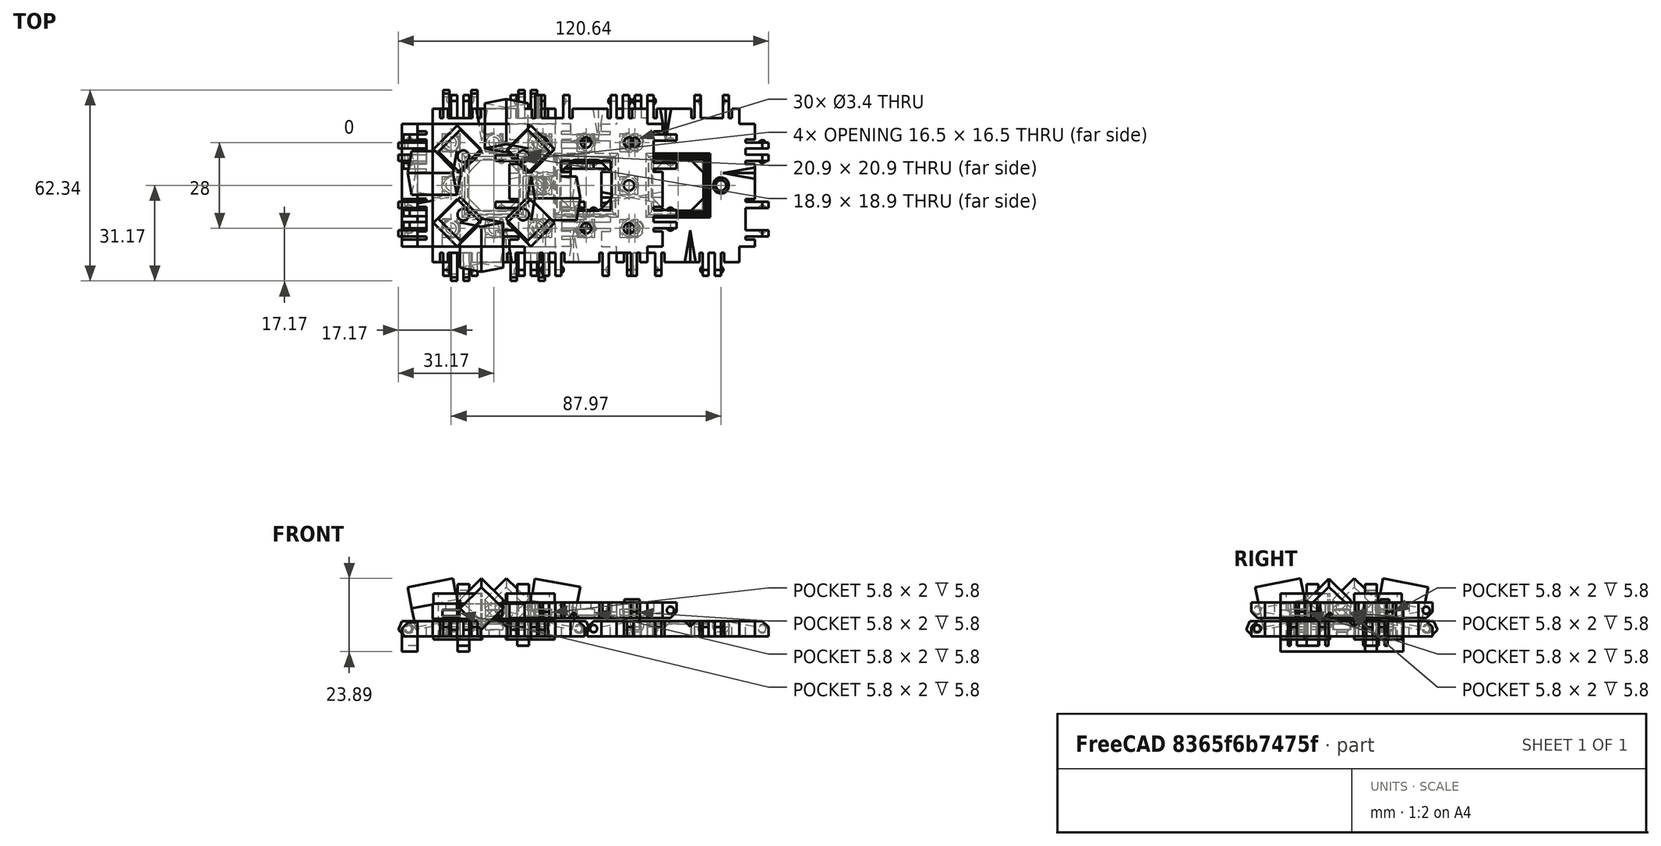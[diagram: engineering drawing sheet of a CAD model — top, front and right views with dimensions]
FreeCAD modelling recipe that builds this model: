
FCSTD DOCUMENT  (FreeCAD 0.17R13522 (Git))
Label: Robot Plates 0.6
License: All rights reserved
LicenseURL: http://en.wikipedia.org/wiki/All_rights_reserved
objects: Part::Box×402, Part::Cut×142, Part::Sphere×126, Part::MultiFuse×90, Part::Fuse×55, Part::Cylinder×40, Part::Chamfer×15, App::DocumentObjectGroup×2, Drawing::FeatureViewAnnotation×2, Drawing::FeaturePage×1
note: 870 computed .brp shape members not serialized (recipe doc carries the construction recipe); baked Part::Feature solids carry a one-line shape summary decoded from their .brp

FEATURE [Part::Box] Box  label="Cube"
  AttacherType = Attacher::AttachEngine3D
  Height = 5
  Length = 40
  Placement = pos=(0,0,-2) rot=(0,0,1;0rad)
  Width = 40
FEATURE [Part::Sphere] Sphere003  label="Mag Hole 3"
  Angle1 = -90
  Angle2 = 90
  Angle3 = 360
  AttacherType = Attacher::AttachEngine3D
  Placement = pos=(6,34,1.7) rot=(0,0,1;0rad)
  Radius = 2.85
FEATURE [Part::Sphere] Sphere005  label="Mag Hole 2"
  Angle1 = -90
  Angle2 = 90
  Angle3 = 360
  AttacherType = Attacher::AttachEngine3D
  Placement = pos=(34,20,1.7) rot=(0,0,1;0rad)
  Radius = 2.85
FEATURE [Part::Sphere] Sphere  label="Mag Hole"
  Angle1 = -90
  Angle2 = 90
  Angle3 = 360
  AttacherType = Attacher::AttachEngine3D
  Placement = pos=(6,6,1.7) rot=(0,0,1;0rad)
  Radius = 2.85
FEATURE [Part::MultiFuse] Fusion004
  Shapes = -> [Sphere,Sphere005,Sphere003]
FEATURE [Part::Cut] Cut003
  Base = -> Box
  Tool = -> Fusion004
FEATURE [Part::Box] Box001  label="Cube001"
  AttacherType = Attacher::AttachEngine3D
  Height = 7
  Length = 5
  Placement = pos=(-5,0,-2) rot=(0,0,1;0rad)
  Width = 40
FEATURE [Part::Box] Box002  label="Cube002"
  AttacherType = Attacher::AttachEngine3D
  Height = 7
  Length = 10
  Placement = pos=(-15,6,-2) rot=(0,0,1;0rad)
  Width = 2
FEATURE [Part::Box] Box003  label="Cube003"
  AttacherType = Attacher::AttachEngine3D
  Height = 7
  Length = 10
  Placement = pos=(-15,10,-2) rot=(0,0,1;0rad)
  Width = 2
FEATURE [Part::Box] Box004  label="Cube004"
  AttacherType = Attacher::AttachEngine3D
  Height = 7
  Length = 10
  Placement = pos=(-15,25.4,-2) rot=(0,0,1;0rad)
  Width = 2
FEATURE [Part::Box] Box005  label="Cube005"
  AttacherType = Attacher::AttachEngine3D
  Height = 7
  Length = 10
  Placement = pos=(-15,34.6,-2) rot=(0,0,1;0rad)
  Width = 2
FEATURE [Part::Sphere] Sphere008
  Angle1 = -90
  Angle2 = 90
  Angle3 = 360
  AttacherType = Attacher::AttachEngine3D
  Placement = pos=(-7.5,6.5,0.5) rot=(0,0,1;0rad)
  Radius = 1.25
FEATURE [Part::Box] Box006  label="Chamfer Cube"
  AttacherType = Attacher::AttachEngine3D
  Height = 10
  Length = 13
  Placement = pos=(-11.69,0,-1.19) rot=(0,-1,0;0.785398rad)
  Width = 40
FEATURE [Part::Sphere] Sphere009
  Angle1 = -90
  Angle2 = 90
  Angle3 = 360
  AttacherType = Attacher::AttachEngine3D
  Placement = pos=(-7.5,11.5,0.5) rot=(0,0,1;0rad)
  Radius = 1.25
FEATURE [Part::Sphere] Sphere010
  Angle1 = -90
  Angle2 = 90
  Angle3 = 360
  AttacherType = Attacher::AttachEngine3D
  Placement = pos=(-7.5,28,0.5) rot=(0,0,1;0rad)
  Radius = 1.5
FEATURE [Part::Sphere] Sphere011
  Angle1 = -90
  Angle2 = 90
  Angle3 = 360
  AttacherType = Attacher::AttachEngine3D
  Placement = pos=(-7.5,34,0.5) rot=(0,0,1;0rad)
  Radius = 1.5
FEATURE [Part::Box] Box007  label="Cube007"
  AttacherType = Attacher::AttachEngine3D
  Height = 7
  Length = 4
  Placement = pos=(-6,5,-2) rot=(0,0,1;0rad)
  Width = 1
FEATURE [Part::Box] Box008  label="Cube008"
  AttacherType = Attacher::AttachEngine3D
  Height = 7
  Length = 4
  Placement = pos=(-6,8,-2) rot=(0,0,1;0rad)
  Width = 2
FEATURE [Part::Box] Box009  label="Cube009"
  AttacherType = Attacher::AttachEngine3D
  Height = 7
  Length = 4
  Placement = pos=(-6,12,-2) rot=(0,0,1;0rad)
  Width = 1
FEATURE [Part::Box] Box010  label="Cube010"
  AttacherType = Attacher::AttachEngine3D
  Height = 7
  Length = 4
  Placement = pos=(-6,24.4,-2) rot=(0,0,1;0rad)
  Width = 1
FEATURE [Part::Box] Box011  label="Cube011"
  AttacherType = Attacher::AttachEngine3D
  Height = 7
  Length = 4
  Placement = pos=(-6,36.6,-2) rot=(0,0,1;0rad)
  Width = 1
FEATURE [Part::Box] Box012  label="Cube012"
  AttacherType = Attacher::AttachEngine3D
  Height = 7
  Length = 4
  Placement = pos=(-6,27.4,-2) rot=(0,0,1;0rad)
  Width = 7.2
FEATURE [Part::MultiFuse] Fusion003  label="Extra Holes for Clips"
  Shapes = -> [Box012,Box009,Box011,Box008,Box010,Box007]
FEATURE [Part::Box] Box013  label="Re-level Edge Clip Block"
  AttacherType = Attacher::AttachEngine3D
  Height = 10
  Length = 20
  Placement = pos=(-19,-2,3) rot=(0,0,1;0rad)
  Width = 44
FEATURE [Part::Box] Box014  label="Cube014"
  AttacherType = Attacher::AttachEngine3D
  Height = 7
  Length = 10
  Placement = pos=(-10,34.6,0) rot=(0,0,1;0rad)
  Width = 2
FEATURE [Part::Box] Box015  label="Cube015"
  AttacherType = Attacher::AttachEngine3D
  Height = 7
  Length = 5
  Width = 40
FEATURE [Part::Box] Box016  label="Cube016"
  AttacherType = Attacher::AttachEngine3D
  Height = 7
  Length = 10
  Placement = pos=(-10,25.4,0) rot=(0,0,1;0rad)
  Width = 2
FEATURE [Part::Box] Box017  label="Cube017"
  AttacherType = Attacher::AttachEngine3D
  Height = 7
  Length = 10
  Placement = pos=(-10,10,0) rot=(0,0,1;0rad)
  Width = 2
FEATURE [Part::Box] Box018  label="Cube018"
  AttacherType = Attacher::AttachEngine3D
  Height = 7
  Length = 10
  Placement = pos=(-10,6,0) rot=(0,0,1;0rad)
  Width = 2
FEATURE [Part::Sphere] Sphere012
  Angle1 = -90
  Angle2 = 90
  Angle3 = 360
  AttacherType = Attacher::AttachEngine3D
  Placement = pos=(-3,6.5,2.5) rot=(0,0,1;0rad)
  Radius = 1.25
FEATURE [Part::Box] Box019  label="Cube019"
  AttacherType = Attacher::AttachEngine3D
  Height = 10
  Length = 13
  Placement = pos=(-10.19,0,-1.19) rot=(0,-1,0;0.785398rad)
  Width = 40
FEATURE [Part::Sphere] Sphere013
  Angle1 = -90
  Angle2 = 90
  Angle3 = 360
  AttacherType = Attacher::AttachEngine3D
  Placement = pos=(-3,11.5,2.5) rot=(0,0,1;0rad)
  Radius = 1.25
FEATURE [Part::Sphere] Sphere014
  Angle1 = -90
  Angle2 = 90
  Angle3 = 360
  AttacherType = Attacher::AttachEngine3D
  Placement = pos=(-3,28,2.5) rot=(0,0,1;0rad)
  Radius = 1.5
FEATURE [Part::Sphere] Sphere015
  Angle1 = -90
  Angle2 = 90
  Angle3 = 360
  AttacherType = Attacher::AttachEngine3D
  Placement = pos=(-3,34,2.5) rot=(0,0,1;0rad)
  Radius = 1.5
FEATURE [Part::MultiFuse] Fusion005
  Shapes = -> [Box015,Box018,Box017,Box016,Box014]
FEATURE [Part::Cut] Cut005
  Base = -> Fusion005
  Tool = -> Box019
FEATURE [Part::MultiFuse] Fusion006
  Shapes = -> [Sphere012,Sphere013,Cut005]
FEATURE [Part::MultiFuse] Fusion007
  Shapes = -> [Sphere015,Sphere014]
FEATURE [Part::Cut] Cut006
  Base = -> Fusion006
  Tool = -> Fusion007
FEATURE [Part::Chamfer] Chamfer002
  Base = -> Cut006
  Edges = 4 edges r=4: [Edge31,Edge37,Edge43,Edge46]
FEATURE [Part::Box] Box020  label="Cube020"
  AttacherType = Attacher::AttachEngine3D
  Height = 7
  Length = 4
  Placement = pos=(-1,5,0) rot=(0,0,1;0rad)
  Width = 1
FEATURE [Part::Box] Box021  label="Cube021"
  AttacherType = Attacher::AttachEngine3D
  Height = 7
  Length = 4
  Placement = pos=(-1,8,0) rot=(0,0,1;0rad)
  Width = 2
FEATURE [Part::Box] Box022  label="Cube022"
  AttacherType = Attacher::AttachEngine3D
  Height = 7
  Length = 4
  Placement = pos=(-1,12,0) rot=(0,0,1;0rad)
  Width = 1
FEATURE [Part::Box] Box023  label="Cube023"
  AttacherType = Attacher::AttachEngine3D
  Height = 7
  Length = 4
  Placement = pos=(-1,24.4,0) rot=(0,0,1;0rad)
  Width = 1
FEATURE [Part::Box] Box024  label="Cube024"
  AttacherType = Attacher::AttachEngine3D
  Height = 7
  Length = 4
  Placement = pos=(-1,36.6,0) rot=(0,0,1;0rad)
  Width = 1
FEATURE [Part::Box] Box025  label="Cube025"
  AttacherType = Attacher::AttachEngine3D
  Height = 7
  Length = 4
  Placement = pos=(-1,27.4,0) rot=(0,0,1;0rad)
  Width = 7.2
FEATURE [Part::MultiFuse] Fusion008
  Shapes = -> [Box025,Box022,Box024,Box021,Box023,Box020]
FEATURE [Part::Cut] Cut007
  Base = -> Chamfer002
  Placement = pos=(-5,40,3) rot=(1,0,0;3.14159rad)
  Tool = -> Fusion008
FEATURE [Part::Box] Box026  label="Cube026"
  AttacherType = Attacher::AttachEngine3D
  Height = 10
  Length = 12
  Placement = pos=(-11,-2,-12) rot=(0,0,1;0rad)
  Width = 44
FEATURE [Part::Cut] Cut008
  Base = -> Cut007
  Placement = pos=(40,0,0) rot=(0,0,1;1.5708rad)
  Tool = -> Box026
FEATURE [Part::Box] Box027  label="Cube027"
  AttacherType = Attacher::AttachEngine3D
  Height = 7
  Length = 4
  Placement = pos=(-1,12,0) rot=(0,0,1;0rad)
  Width = 1
FEATURE [Part::Box] Box028  label="Cube028"
  AttacherType = Attacher::AttachEngine3D
  Height = 10
  Length = 13
  Placement = pos=(-10.19,0,-1.19) rot=(0,-1,0;0.785398rad)
  Width = 40
FEATURE [Part::Box] Box029  label="Cube029"
  AttacherType = Attacher::AttachEngine3D
  Height = 7
  Length = 4
  Placement = pos=(-1,27.4,0) rot=(0,0,1;0rad)
  Width = 7.2
FEATURE [Part::Box] Box030  label="Cube030"
  AttacherType = Attacher::AttachEngine3D
  Height = 7
  Length = 4
  Placement = pos=(-1,5,0) rot=(0,0,1;0rad)
  Width = 1
FEATURE [Part::Box] Box031  label="Cube031"
  AttacherType = Attacher::AttachEngine3D
  Height = 7
  Length = 10
  Placement = pos=(-10,6,0) rot=(0,0,1;0rad)
  Width = 2
FEATURE [Part::Box] Box032  label="Cube032"
  AttacherType = Attacher::AttachEngine3D
  Height = 10
  Length = 12
  Placement = pos=(-11,-2,-12) rot=(0,0,1;0rad)
  Width = 44
FEATURE [Part::Sphere] Sphere016
  Angle1 = -90
  Angle2 = 90
  Angle3 = 360
  AttacherType = Attacher::AttachEngine3D
  Placement = pos=(-3,6.5,2.5) rot=(0,0,1;0rad)
  Radius = 1.25
FEATURE [Part::Box] Box033  label="Cube033"
  AttacherType = Attacher::AttachEngine3D
  Height = 7
  Length = 10
  Placement = pos=(-10,25.4,0) rot=(0,0,1;0rad)
  Width = 2
FEATURE [Part::Box] Box034  label="Cube034"
  AttacherType = Attacher::AttachEngine3D
  Height = 7
  Length = 10
  Placement = pos=(-10,10,0) rot=(0,0,1;0rad)
  Width = 2
FEATURE [Part::Sphere] Sphere017
  Angle1 = -90
  Angle2 = 90
  Angle3 = 360
  AttacherType = Attacher::AttachEngine3D
  Placement = pos=(-3,28,2.5) rot=(0,0,1;0rad)
  Radius = 1.5
FEATURE [Part::Sphere] Sphere018
  Angle1 = -90
  Angle2 = 90
  Angle3 = 360
  AttacherType = Attacher::AttachEngine3D
  Placement = pos=(-3,11.5,2.5) rot=(0,0,1;0rad)
  Radius = 1.25
FEATURE [Part::Box] Box035  label="Cube035"
  AttacherType = Attacher::AttachEngine3D
  Height = 7
  Length = 4
  Placement = pos=(-1,36.6,0) rot=(0,0,1;0rad)
  Width = 1
FEATURE [Part::Sphere] Sphere019
  Angle1 = -90
  Angle2 = 90
  Angle3 = 360
  AttacherType = Attacher::AttachEngine3D
  Placement = pos=(-3,34,2.5) rot=(0,0,1;0rad)
  Radius = 1.5
FEATURE [Part::MultiFuse] Fusion011
  Shapes = -> [Sphere019,Sphere017]
FEATURE [Part::Box] Box036  label="Cube036"
  AttacherType = Attacher::AttachEngine3D
  Height = 7
  Length = 4
  Placement = pos=(-1,8,0) rot=(0,0,1;0rad)
  Width = 2
FEATURE [Part::Box] Box037  label="Cube037"
  AttacherType = Attacher::AttachEngine3D
  Height = 7
  Length = 10
  Placement = pos=(-10,34.6,0) rot=(0,0,1;0rad)
  Width = 2
FEATURE [Part::Box] Box038  label="Cube038"
  AttacherType = Attacher::AttachEngine3D
  Height = 7
  Length = 4
  Placement = pos=(-1,24.4,0) rot=(0,0,1;0rad)
  Width = 1
FEATURE [Part::MultiFuse] Fusion009
  Shapes = -> [Box029,Box027,Box035,Box036,Box038,Box030]
FEATURE [Part::Box] Box039  label="Cube039"
  AttacherType = Attacher::AttachEngine3D
  Height = 7
  Length = 5
  Width = 40
FEATURE [Part::MultiFuse] Fusion012
  Shapes = -> [Box039,Box031,Box034,Box033,Box037]
FEATURE [Part::Cut] Cut011
  Base = -> Fusion012
  Tool = -> Box028
FEATURE [Part::MultiFuse] Fusion010
  Shapes = -> [Sphere016,Sphere018,Cut011]
FEATURE [Part::Cut] Cut012
  Base = -> Fusion010
  Tool = -> Fusion011
FEATURE [Part::Chamfer] Chamfer003
  Base = -> Cut012
  Edges = 4 edges r=4: [Edge31,Edge37,Edge43,Edge46]
FEATURE [Part::Cut] Cut010
  Base = -> Chamfer003
  Placement = pos=(-5,40,3) rot=(1,0,0;3.14159rad)
  Tool = -> Fusion009
FEATURE [Part::Cut] Cut009
  Base = -> Cut010
  Placement = pos=(40,40,0) rot=(0,0,1;3.14159rad)
  Tool = -> Box032
FEATURE [Part::Sphere] Sphere020
  Angle1 = -90
  Angle2 = 90
  Angle3 = 360
  AttacherType = Attacher::AttachEngine3D
  Placement = pos=(-3,11.5,2.5) rot=(0,0,1;0rad)
  Radius = 1.25
FEATURE [Part::Box] Box040  label="Cube040"
  AttacherType = Attacher::AttachEngine3D
  Height = 7
  Length = 10
  Placement = pos=(-10,6,0) rot=(0,0,1;0rad)
  Width = 2
FEATURE [Part::Box] Box041  label="Cube041"
  AttacherType = Attacher::AttachEngine3D
  Height = 7
  Length = 4
  Placement = pos=(-1,8,0) rot=(0,0,1;0rad)
  Width = 2
FEATURE [Part::Box] Box042  label="Cube042"
  AttacherType = Attacher::AttachEngine3D
  Height = 7
  Length = 10
  Placement = pos=(-10,10,0) rot=(0,0,1;0rad)
  Width = 2
FEATURE [Part::Box] Box043  label="Cube043"
  AttacherType = Attacher::AttachEngine3D
  Height = 10
  Length = 12
  Placement = pos=(-11,-2,-12) rot=(0,0,1;0rad)
  Width = 44
FEATURE [Part::Box] Box044  label="Cube044"
  AttacherType = Attacher::AttachEngine3D
  Height = 7
  Length = 4
  Placement = pos=(-1,5,0) rot=(0,0,1;0rad)
  Width = 1
FEATURE [Part::Sphere] Sphere021
  Angle1 = -90
  Angle2 = 90
  Angle3 = 360
  AttacherType = Attacher::AttachEngine3D
  Placement = pos=(-3,28,2.5) rot=(0,0,1;0rad)
  Radius = 1.5
FEATURE [Part::Sphere] Sphere022
  Angle1 = -90
  Angle2 = 90
  Angle3 = 360
  AttacherType = Attacher::AttachEngine3D
  Placement = pos=(-3,6.5,2.5) rot=(0,0,1;0rad)
  Radius = 1.25
FEATURE [Part::Sphere] Sphere023
  Angle1 = -90
  Angle2 = 90
  Angle3 = 360
  AttacherType = Attacher::AttachEngine3D
  Placement = pos=(-3,34,2.5) rot=(0,0,1;0rad)
  Radius = 1.5
FEATURE [Part::Box] Box045  label="Cube045"
  AttacherType = Attacher::AttachEngine3D
  Height = 7
  Length = 4
  Placement = pos=(-1,12,0) rot=(0,0,1;0rad)
  Width = 1
FEATURE [Part::Box] Box046  label="Cube046"
  AttacherType = Attacher::AttachEngine3D
  Height = 7
  Length = 5
  Width = 40
FEATURE [Part::Box] Box047  label="Cube047"
  AttacherType = Attacher::AttachEngine3D
  Height = 7
  Length = 4
  Placement = pos=(-1,36.6,0) rot=(0,0,1;0rad)
  Width = 1
FEATURE [Part::Box] Box048  label="Cube048"
  AttacherType = Attacher::AttachEngine3D
  Height = 7
  Length = 4
  Placement = pos=(-1,24.4,0) rot=(0,0,1;0rad)
  Width = 1
FEATURE [Part::Box] Box049  label="Cube049"
  AttacherType = Attacher::AttachEngine3D
  Height = 7
  Length = 10
  Placement = pos=(-10,25.4,0) rot=(0,0,1;0rad)
  Width = 2
FEATURE [Part::Box] Box050  label="Cube050"
  AttacherType = Attacher::AttachEngine3D
  Height = 10
  Length = 13
  Placement = pos=(-10.19,0,-1.19) rot=(0,-1,0;0.785398rad)
  Width = 40
FEATURE [Part::Box] Box051  label="Cube051"
  AttacherType = Attacher::AttachEngine3D
  Height = 7
  Length = 10
  Placement = pos=(-10,34.6,0) rot=(0,0,1;0rad)
  Width = 2
FEATURE [Part::MultiFuse] Fusion015
  Shapes = -> [Box046,Box040,Box042,Box049,Box051]
FEATURE [Part::Cut] Cut013
  Base = -> Fusion015
  Tool = -> Box050
FEATURE [Part::MultiFuse] Fusion013
  Shapes = -> [Sphere022,Sphere020,Cut013]
FEATURE [Part::MultiFuse] Fusion016
  Shapes = -> [Sphere023,Sphere021]
FEATURE [Part::Cut] Cut014
  Base = -> Fusion013
  Tool = -> Fusion016
FEATURE [Part::Chamfer] Chamfer004
  Base = -> Cut014
  Edges = 4 edges r=4: [Edge31,Edge37,Edge43,Edge46]
FEATURE [Part::Box] Box052  label="Cube052"
  AttacherType = Attacher::AttachEngine3D
  Height = 7
  Length = 4
  Placement = pos=(-1,27.4,0) rot=(0,0,1;0rad)
  Width = 7.2
FEATURE [Part::MultiFuse] Fusion014
  Shapes = -> [Box052,Box045,Box047,Box041,Box048,Box044]
FEATURE [Part::Cut] Cut016
  Base = -> Chamfer004
  Placement = pos=(-5,40,3) rot=(1,0,0;3.14159rad)
  Tool = -> Fusion014
FEATURE [Part::Cut] Cut015
  Base = -> Cut016
  Placement = pos=(0,40,0) rot=(0,0,-1;1.5708rad)
  Tool = -> Box043
FEATURE [Part::Box] Box054  label="Cube054"
  AttacherType = Attacher::AttachEngine3D
  Height = 15
  Length = 10
  Placement = pos=(9,2,-3) rot=(0,0,1;0.785398rad)
  Width = 10
FEATURE [Part::Box] Box055  label="Cube055"
  AttacherType = Attacher::AttachEngine3D
  Height = 15
  Length = 10
  Placement = pos=(31,24,-3) rot=(0,0,1;0.785398rad)
  Width = 10
FEATURE [Part::Box] Box056  label="Cube056"
  AttacherType = Attacher::AttachEngine3D
  Height = 15
  Length = 10
  Placement = pos=(31,2,-3) rot=(0,0,1;0.785398rad)
  Width = 10
FEATURE [Part::Box] Box057  label="Cube057"
  AttacherType = Attacher::AttachEngine3D
  Height = 15
  Length = 10
  Placement = pos=(9,24,-3) rot=(0,0,1;0.785398rad)
  Width = 10
FEATURE [Part::MultiFuse] Fusion017
  Shapes = -> [Box054,Box057,Box056,Box055]
FEATURE [Part::Box] Box058  label="Cube058"
  AttacherType = Attacher::AttachEngine3D
  Height = 5
  Length = 40
  Placement = pos=(0,0,3.7) rot=(0,0,1;0rad)
  Width = 40
FEATURE [Part::Box] Box059  label="Square Nut Hole 008"
  AttacherType = Attacher::AttachEngine3D
  Height = 2
  Length = 5.6
  Placement = pos=(17.2,31.2,4.6) rot=(0,0,1;0rad)
  Width = 5.6
FEATURE [Part::Box] Box060  label="Square Nut Hole 009"
  AttacherType = Attacher::AttachEngine3D
  Height = 2
  Length = 5.6
  Placement = pos=(17.2,-0.85,4.6) rot=(0,0,1;0rad)
  Width = 10
FEATURE [Part::Box] Box061  label="Square Nut Hole 010"
  AttacherType = Attacher::AttachEngine3D
  Height = 2
  Length = 5.6
  Placement = pos=(31.2,-0.85,4.6) rot=(0,0,1;0rad)
  Width = 10
FEATURE [Part::Box] Box062  label="Square Nut Hole 011"
  AttacherType = Attacher::AttachEngine3D
  Height = 2
  Length = 5.4
  Placement = pos=(31.3,17.3,4.6) rot=(0,0,1;0rad)
  Width = 5.4
FEATURE [Part::Box] Box063  label="Square Nut Hole 012"
  AttacherType = Attacher::AttachEngine3D
  Height = 2
  Length = 5.7
  Placement = pos=(3.15,31.15,4.6) rot=(0,0,1;0rad)
  Width = 5.7
FEATURE [Part::Box] Box064  label="Square Nut Hole 013"
  AttacherType = Attacher::AttachEngine3D
  Height = 2
  Length = 5.5
  Placement = pos=(31.25,31.25,4.6) rot=(0,0,1;0rad)
  Width = 5.5
FEATURE [Part::Box] Box065  label="Square Nut Hole 014"
  AttacherType = Attacher::AttachEngine3D
  Height = 2
  Length = 5.8
  Placement = pos=(3.1,17.1,4.6) rot=(0,0,1;0rad)
  Width = 5.8
FEATURE [Part::Box] Box066  label="Square Nut Hole 015"
  AttacherType = Attacher::AttachEngine3D
  Height = 2
  Length = 5.6
  Placement = pos=(3.2,-0.85,4.6) rot=(0,0,1;0rad)
  Width = 10
FEATURE [Part::Sphere] Sphere006  label="Nut Clearence1"
  Angle1 = -90
  Angle2 = 90
  Angle3 = 360
  AttacherType = Attacher::AttachEngine3D
  Placement = pos=(6,6,2.4) rot=(0,0,1;0rad)
  Radius = 3.35
FEATURE [Part::Sphere] Sphere024
  Angle1 = -90
  Angle2 = 90
  Angle3 = 360
  AttacherType = Attacher::AttachEngine3D
  Placement = pos=(6,34,2.4) rot=(0,0,1;0rad)
  Radius = 3.35
FEATURE [Part::Sphere] Sphere007
  Angle1 = -90
  Angle2 = 90
  Angle3 = 360
  AttacherType = Attacher::AttachEngine3D
  Placement = pos=(34,20,2.4) rot=(0,0,1;0rad)
  Radius = 3.35
FEATURE [Part::Sphere] Sphere001
  Angle1 = -90
  Angle2 = 90
  Angle3 = 360
  AttacherType = Attacher::AttachEngine3D
  Placement = pos=(34,6,2.4) rot=(0,0,1;0rad)
  Radius = 3.35
FEATURE [Part::Sphere] Sphere025
  Angle1 = -90
  Angle2 = 90
  Angle3 = 360
  AttacherType = Attacher::AttachEngine3D
  Placement = pos=(20,6,2.4) rot=(0,0,1;0rad)
  Radius = 3.35
FEATURE [Part::Sphere] Sphere026
  Angle1 = -90
  Angle2 = 90
  Angle3 = 360
  AttacherType = Attacher::AttachEngine3D
  Placement = pos=(20,34,2.4) rot=(0,0,1;0rad)
  Radius = 3.35
FEATURE [Part::Sphere] Sphere004
  Angle1 = -90
  Angle2 = 90
  Angle3 = 360
  AttacherType = Attacher::AttachEngine3D
  Placement = pos=(6,20,2.4) rot=(0,0,1;0rad)
  Radius = 3.35
FEATURE [Part::Sphere] Sphere002
  Angle1 = -90
  Angle2 = 90
  Angle3 = 360
  AttacherType = Attacher::AttachEngine3D
  Placement = pos=(34,34,2.4) rot=(0,0,1;0rad)
  Radius = 3.35
FEATURE [Part::Cylinder] Cylinder
  Angle = 360
  AttacherType = Attacher::AttachEngine3D
  Height = 10
  Placement = pos=(6,6,0) rot=(0,0,1;0rad)
  Radius = 1.7
FEATURE [Part::Cylinder] Cylinder002
  Angle = 360
  AttacherType = Attacher::AttachEngine3D
  Height = 10
  Placement = pos=(34,6,0) rot=(0,0,1;0rad)
  Radius = 1.7
FEATURE [Part::Cylinder] Cylinder001
  Angle = 360
  AttacherType = Attacher::AttachEngine3D
  Height = 10
  Placement = pos=(20,6,0) rot=(0,0,1;0rad)
  Radius = 1.7
FEATURE [Part::Cylinder] Cylinder003
  Angle = 360
  AttacherType = Attacher::AttachEngine3D
  Height = 10
  Placement = pos=(34,34,0) rot=(0,0,1;0rad)
  Radius = 1.7
FEATURE [Part::Cylinder] Cylinder004
  Angle = 360
  AttacherType = Attacher::AttachEngine3D
  Height = 10
  Placement = pos=(20,34,0) rot=(0,0,1;0rad)
  Radius = 1.7
FEATURE [Part::Cylinder] Cylinder005
  Angle = 360
  AttacherType = Attacher::AttachEngine3D
  Height = 10
  Placement = pos=(6,34,0) rot=(0,0,1;0rad)
  Radius = 1.7
FEATURE [Part::Cylinder] Cylinder006
  Angle = 360
  AttacherType = Attacher::AttachEngine3D
  Height = 10
  Placement = pos=(6,20,0) rot=(0,0,1;0rad)
  Radius = 1.7
FEATURE [Part::Cylinder] Cylinder007
  Angle = 360
  AttacherType = Attacher::AttachEngine3D
  Height = 10
  Placement = pos=(34,20,0) rot=(0,0,1;0rad)
  Radius = 1.7
FEATURE [Part::MultiFuse] Fusion018
  Shapes = -> [Cylinder,Cylinder004,Cylinder007,Cylinder005,Cylinder006,Cylinder001,Cylinder002,Cylinder003]
FEATURE [Part::MultiFuse] Fusion019
  Shapes = -> [Sphere007,Sphere024,Sphere006,Sphere025,Sphere001,Sphere026,Sphere004,Sphere002]
FEATURE [Part::MultiFuse] Fusion020
  Shapes = -> [Box061,Box065,Box062,Box063,Box064,Box066,Box059,Box060]
FEATURE [Part::Cut] Cut017
  Base = -> Box058
  Tool = -> Fusion020
FEATURE [Part::Cut] Cut019
  Base = -> Cut017
  Tool = -> Fusion019
FEATURE [Part::Cut] Cut018
  Base = -> Cut019
  Tool = -> Fusion018
FEATURE [Part::Cylinder] Cylinder008
  Angle = 360
  AttacherType = Attacher::AttachEngine3D
  Height = 20
  Placement = pos=(10,10.5,-5) rot=(0,0,1;0rad)
  Radius = 1.9
FEATURE [Part::Cylinder] Cylinder009
  Angle = 360
  AttacherType = Attacher::AttachEngine3D
  Height = 20
  Placement = pos=(29.5,10.5,-5) rot=(0,0,1;0rad)
  Radius = 1.9
FEATURE [Part::Cylinder] Cylinder010
  Angle = 360
  AttacherType = Attacher::AttachEngine3D
  Height = 20
  Placement = pos=(29.5,29.5,-5) rot=(0,0,1;0rad)
  Radius = 1.9
FEATURE [Part::Cylinder] Cylinder011
  Angle = 360
  AttacherType = Attacher::AttachEngine3D
  Height = 20
  Placement = pos=(10,29.5,-7) rot=(0,0,1;0rad)
  Radius = 1.9
FEATURE [Part::MultiFuse] Fusion021  label="M2 Screw holes"
  Shapes = -> [Cylinder008,Cylinder009,Cylinder011,Cylinder010]
FEATURE [Part::Box] Box067  label="Square Nut Hole 016"
  AttacherType = Attacher::AttachEngine3D
  Height = 2
  Length = 5.8
  Placement = pos=(31.1,17.1,4.6) rot=(0,0,1;0rad)
  Width = 5.8
FEATURE [Part::Box] Box068  label="Square Nut Hole 017"
  AttacherType = Attacher::AttachEngine3D
  Height = 2
  Length = 5.8
  Placement = pos=(17.1,3.1,4.6) rot=(0,0,1;0rad)
  Width = 5.8
FEATURE [Part::Box] Box069  label="Square Nut Hole 018"
  AttacherType = Attacher::AttachEngine3D
  Height = 2
  Length = 5.8
  Placement = pos=(31.1,3.1,4.6) rot=(0,0,1;0rad)
  Width = 5.8
FEATURE [Part::Box] Box070  label="Square Nut Hole 019"
  AttacherType = Attacher::AttachEngine3D
  Height = 2
  Length = 5.8
  Placement = pos=(3.1,3.1,4.6) rot=(0,0,1;0rad)
  Width = 5.8
FEATURE [Part::Box] Box071  label="Square Nut Hole 020"
  AttacherType = Attacher::AttachEngine3D
  Height = 2
  Length = 5.8
  Placement = pos=(3.1,31.1,4.6) rot=(0,0,1;0rad)
  Width = 5.8
FEATURE [Part::Box] Box072  label="Square Nut Hole 021"
  AttacherType = Attacher::AttachEngine3D
  Height = 2
  Length = 5.8
  Placement = pos=(17.1,31.1,4.6) rot=(0,0,1;0rad)
  Width = 5.8
FEATURE [Part::Box] Box073  label="Square Nut Hole 022"
  AttacherType = Attacher::AttachEngine3D
  Height = 2
  Length = 5.8
  Placement = pos=(31.1,31.1,4.6) rot=(0,0,1;0rad)
  Width = 5.8
FEATURE [Part::Box] Box074  label="Square Nut Hole 023"
  AttacherType = Attacher::AttachEngine3D
  Height = 2
  Length = 5.8
  Placement = pos=(3.1,17.1,4.6) rot=(0,0,1;0rad)
  Width = 5.8
FEATURE [Part::Cylinder] Cylinder012
  Angle = 360
  AttacherType = Attacher::AttachEngine3D
  Height = 10
  Placement = pos=(6,6,0) rot=(0,0,1;0rad)
  Radius = 1.7
FEATURE [Part::Cylinder] Cylinder013
  Angle = 360
  AttacherType = Attacher::AttachEngine3D
  Height = 10
  Placement = pos=(34,34,0) rot=(0,0,1;0rad)
  Radius = 1.7
FEATURE [Part::Cylinder] Cylinder014
  Angle = 360
  AttacherType = Attacher::AttachEngine3D
  Height = 10
  Placement = pos=(20,34,0) rot=(0,0,1;0rad)
  Radius = 1.7
FEATURE [Part::Cylinder] Cylinder015
  Angle = 360
  AttacherType = Attacher::AttachEngine3D
  Height = 10
  Placement = pos=(6,34,0) rot=(0,0,1;0rad)
  Radius = 1.7
FEATURE [Part::Cylinder] Cylinder016
  Angle = 360
  AttacherType = Attacher::AttachEngine3D
  Height = 10
  Placement = pos=(6,20,0) rot=(0,0,1;0rad)
  Radius = 1.7
FEATURE [Part::Cylinder] Cylinder017
  Angle = 360
  AttacherType = Attacher::AttachEngine3D
  Height = 10
  Placement = pos=(34,20,0) rot=(0,0,1;0rad)
  Radius = 1.7
FEATURE [Part::Cylinder] Cylinder018
  Angle = 360
  AttacherType = Attacher::AttachEngine3D
  Height = 10
  Placement = pos=(34,6,0) rot=(0,0,1;0rad)
  Radius = 1.7
FEATURE [Part::Cylinder] Cylinder019
  Angle = 360
  AttacherType = Attacher::AttachEngine3D
  Height = 10
  Placement = pos=(20,6,0) rot=(0,0,1;0rad)
  Radius = 1.7
FEATURE [Part::Box] Box075  label="Cube059"
  AttacherType = Attacher::AttachEngine3D
  Height = 5
  Length = 40
  Placement = pos=(0,0,-2) rot=(0,0,1;0rad)
  Width = 40
FEATURE [Part::Sphere] Sphere027
  Angle1 = -90
  Angle2 = 90
  Angle3 = 360
  AttacherType = Attacher::AttachEngine3D
  Placement = pos=(34,20,2.4) rot=(0,0,1;0rad)
  Radius = 3.35
FEATURE [Part::Sphere] Sphere028  label="Nut Clearence002"
  Angle1 = -90
  Angle2 = 90
  Angle3 = 360
  AttacherType = Attacher::AttachEngine3D
  Placement = pos=(6,6,2.4) rot=(0,0,1;0rad)
  Radius = 3.35
FEATURE [Part::Sphere] Sphere029
  Angle1 = -90
  Angle2 = 90
  Angle3 = 360
  AttacherType = Attacher::AttachEngine3D
  Placement = pos=(34,34,2.4) rot=(0,0,1;0rad)
  Radius = 3.35
FEATURE [Part::Sphere] Sphere030
  Angle1 = -90
  Angle2 = 90
  Angle3 = 360
  AttacherType = Attacher::AttachEngine3D
  Placement = pos=(34,6,2.4) rot=(0,0,1;0rad)
  Radius = 3.35
FEATURE [Part::Sphere] Sphere031
  Angle1 = -90
  Angle2 = 90
  Angle3 = 360
  AttacherType = Attacher::AttachEngine3D
  Placement = pos=(20,6,2.4) rot=(0,0,1;0rad)
  Radius = 3.35
FEATURE [Part::Sphere] Sphere032
  Angle1 = -90
  Angle2 = 90
  Angle3 = 360
  AttacherType = Attacher::AttachEngine3D
  Placement = pos=(6,34,2.4) rot=(0,0,1;0rad)
  Radius = 3.35
FEATURE [Part::Sphere] Sphere033
  Angle1 = -90
  Angle2 = 90
  Angle3 = 360
  AttacherType = Attacher::AttachEngine3D
  Placement = pos=(6,20,2.4) rot=(0,0,1;0rad)
  Radius = 3.35
FEATURE [Part::Sphere] Sphere034
  Angle1 = -90
  Angle2 = 90
  Angle3 = 360
  AttacherType = Attacher::AttachEngine3D
  Placement = pos=(20,34,2.4) rot=(0,0,1;0rad)
  Radius = 3.35
FEATURE [Part::Box] Box076  label="Cube060"
  AttacherType = Attacher::AttachEngine3D
  Height = 15
  Length = 16.5
  Placement = pos=(11.75,11.75,-3) rot=(0,0,1;0rad)
  Width = 16.5
FEATURE [Part::Box] Box077  label="Cube061"
  AttacherType = Attacher::AttachEngine3D
  Height = 15
  Length = 11
  Placement = pos=(8,24,-3) rot=(0,0,1;0.785398rad)
  Width = 11
FEATURE [Part::Box] Box078  label="Cube062"
  AttacherType = Attacher::AttachEngine3D
  Height = 15
  Length = 11
  Placement = pos=(8,0,-3) rot=(0,0,1;0.785398rad)
  Width = 11
FEATURE [Part::Box] Box079  label="Cube063"
  AttacherType = Attacher::AttachEngine3D
  Height = 15
  Length = 11
  Placement = pos=(32,0,-3) rot=(0,0,1;0.785398rad)
  Width = 11
FEATURE [Part::Box] Box080  label="Cube064"
  AttacherType = Attacher::AttachEngine3D
  Height = 15
  Length = 11
  Placement = pos=(32,24,-3) rot=(0,0,1;0.785398rad)
  Width = 11
FEATURE [Part::MultiFuse] Fusion022
  Shapes = -> [Box078,Box077,Box079,Box080]
FEATURE [Part::Cylinder] Cylinder020
  Angle = 360
  AttacherType = Attacher::AttachEngine3D
  Height = 20
  Placement = pos=(29.5,10.5,-5) rot=(0,0,1;0rad)
  Radius = 1.9
FEATURE [Part::Cylinder] Cylinder021
  Angle = 360
  AttacherType = Attacher::AttachEngine3D
  Height = 20
  Placement = pos=(10,29.5,-7) rot=(0,0,1;0rad)
  Radius = 1.9
FEATURE [Part::Cylinder] Cylinder022
  Angle = 360
  AttacherType = Attacher::AttachEngine3D
  Height = 20
  Placement = pos=(10,10.5,-5) rot=(0,0,1;0rad)
  Radius = 1.9
FEATURE [Part::Cylinder] Cylinder023
  Angle = 360
  AttacherType = Attacher::AttachEngine3D
  Height = 20
  Placement = pos=(29.5,29.5,-5) rot=(0,0,1;0rad)
  Radius = 1.9
FEATURE [Part::MultiFuse] Fusion023  label="M2 Screw holes001"
  Shapes = -> [Cylinder022,Cylinder020,Cylinder021,Cylinder023]
FEATURE [Part::MultiFuse] Fusion024  label="Square Nut Hole"
  Shapes = -> [Box067,Box073,Box071,Box069,Box068,Box070,Box072,Box074]
FEATURE [Part::MultiFuse] Fusion025  label="Square Nut Screw Holes"
  Shapes = -> [Cylinder012,Cylinder018,Cylinder016,Cylinder015,Cylinder014,Cylinder013,Cylinder017,Cylinder019]
FEATURE [Part::MultiFuse] Fusion026  label="Nut Chamfers"
  Shapes = -> [Sphere027,Sphere028,Sphere029,Sphere031,Sphere032,Sphere033,Sphere034,Sphere030]
FEATURE [App::DocumentObjectGroup] Group  label="Cubes"
  Group = -> [Fusion017,Fusion022]
FEATURE [Part::Box] Box083  label="Cube067"
  AttacherType = Attacher::AttachEngine3D
  Height = 10
  Length = 21
  Placement = pos=(9.5,9.5,2.1) rot=(0,0,1;0rad)
  Width = 21
FEATURE [Part::Box] Box084  label="Cube068"
  AttacherType = Attacher::AttachEngine3D
  Height = 14
  Length = 17
  Placement = pos=(11.5,11.5,0) rot=(0,0,1;0rad)
  Width = 17
FEATURE [Part::Cut] Cut020
  Base = -> Box083
  Tool = -> Box084
FEATURE [Part::Chamfer] Chamfer007
  Base = -> Cut020
  Edges = 8 edges r=0.95: [Edge4,Edge5,Edge14,Edge16,Edge17,Edge18,Edge19,Edge20]
FEATURE [Part::Chamfer] Chamfer008
  Base = -> Box076
  Edges = 4 edges r=4: [Edge1,Edge3,Edge5,Edge7]
FEATURE [Part::Box] Box085  label="Cube069"
  AttacherType = Attacher::AttachEngine3D
  Height = 15
  Length = 16
  Placement = pos=(12,12,-13) rot=(0,0,1;0rad)
  Width = 16
FEATURE [Part::Box] Box086  label="Cube070"
  AttacherType = Attacher::AttachEngine3D
  Height = 10
  Length = 10
  Placement = pos=(24,-6,1) rot=(0.205904,-0.974848,-0.085288;0.803573rad)
  Width = 15
FEATURE [Part::Box] Box089  label="Cube073"
  AttacherType = Attacher::AttachEngine3D
  Height = 10
  Length = 10
  Placement = pos=(17,32.0919,9.95) rot=(-0.225436,0.969773,-0.093378;0.807337rad)
  Width = 15
FEATURE [Part::Box] Box090  label="Cube074"
  AttacherType = Attacher::AttachEngine3D
  Height = 10
  Length = 15
  Placement = pos=(30.8481,15.8,2.86019) rot=(0.974848,0.205904,-0.085288;0.803573rad)
  Width = 10
FEATURE [Part::Box] Box091  label="Cube075"
  AttacherType = Attacher::AttachEngine3D
  Height = 10
  Length = 10
  Placement = pos=(7.9081,17,9.95) rot=(-0.450607,0.280623,0.847469;1.65638rad)
  Width = 15
FEATURE [Part::Box] Box092  label="Cube076"
  AttacherType = Attacher::AttachEngine3D
  Height = 10
  Length = 10
  Placement = pos=(23,7.9081,9.95) rot=(-0.381178,-0.08861,0.920245;3.06822rad)
  Width = 15
FEATURE [Part::Box] Box093  label="Cube077"
  AttacherType = Attacher::AttachEngine3D
  Height = 7
  Length = 5
  Width = 40
FEATURE [Part::Box] Box094  label="Cube078"
  AttacherType = Attacher::AttachEngine3D
  Height = 7
  Length = 10
  Placement = pos=(-10,6,0) rot=(0,0,1;0rad)
  Width = 2
FEATURE [Part::Box] Box095  label="Cube079"
  AttacherType = Attacher::AttachEngine3D
  Height = 7
  Length = 10
  Placement = pos=(-10,10,0) rot=(0,0,1;0rad)
  Width = 2
FEATURE [Part::Box] Box096  label="Cube080"
  AttacherType = Attacher::AttachEngine3D
  Height = 7
  Length = 10
  Placement = pos=(-10,25.4,0) rot=(0,0,1;0rad)
  Width = 2
FEATURE [Part::Box] Box097  label="Cube081"
  AttacherType = Attacher::AttachEngine3D
  Height = 7
  Length = 10
  Placement = pos=(-10,34.6,0) rot=(0,0,1;0rad)
  Width = 2
FEATURE [Part::Sphere] Sphere035
  Angle1 = -90
  Angle2 = 90
  Angle3 = 360
  AttacherType = Attacher::AttachEngine3D
  Placement = pos=(-3,6.5,2.5) rot=(0,0,1;0rad)
  Radius = 1.25
FEATURE [Part::Box] Box098  label="Cube082"
  AttacherType = Attacher::AttachEngine3D
  Height = 10
  Length = 13
  Placement = pos=(-10.19,0,-1.19) rot=(0,-1,0;0.785398rad)
  Width = 40
FEATURE [Part::Sphere] Sphere036
  Angle1 = -90
  Angle2 = 90
  Angle3 = 360
  AttacherType = Attacher::AttachEngine3D
  Placement = pos=(-3,11.5,2.5) rot=(0,0,1;0rad)
  Radius = 1.25
FEATURE [Part::Sphere] Sphere037
  Angle1 = -90
  Angle2 = 90
  Angle3 = 360
  AttacherType = Attacher::AttachEngine3D
  Placement = pos=(-3,28,2.5) rot=(0,0,1;0rad)
  Radius = 1.5
FEATURE [Part::Sphere] Sphere038
  Angle1 = -90
  Angle2 = 90
  Angle3 = 360
  AttacherType = Attacher::AttachEngine3D
  Placement = pos=(-3,34,2.5) rot=(0,0,1;0rad)
  Radius = 1.5
FEATURE [Part::MultiFuse] Fusion030
  Shapes = -> [Box093,Box094,Box095,Box096,Box097]
FEATURE [Part::Cut] Cut025
  Base = -> Fusion030
  Tool = -> Box098
FEATURE [Part::MultiFuse] Fusion031
  Shapes = -> [Sphere035,Sphere036,Cut025]
FEATURE [Part::MultiFuse] Fusion032
  Shapes = -> [Sphere038,Sphere037]
FEATURE [Part::Cut] Cut026
  Base = -> Fusion031
  Tool = -> Fusion032
FEATURE [Part::Chamfer] Chamfer009
  Base = -> Cut026
  Edges = 4 edges r=4: [Edge31,Edge37,Edge43,Edge46]
FEATURE [Part::Box] Box099  label="Cube083"
  AttacherType = Attacher::AttachEngine3D
  Height = 7
  Length = 4
  Placement = pos=(-1,5,0) rot=(0,0,1;0rad)
  Width = 1
FEATURE [Part::Box] Box100  label="Cube084"
  AttacherType = Attacher::AttachEngine3D
  Height = 7
  Length = 4
  Placement = pos=(-1,8,0) rot=(0,0,1;0rad)
  Width = 2
FEATURE [Part::Box] Box101  label="Cube085"
  AttacherType = Attacher::AttachEngine3D
  Height = 7
  Length = 4
  Placement = pos=(-1,12,0) rot=(0,0,1;0rad)
  Width = 1
FEATURE [Part::Box] Box102  label="Cube086"
  AttacherType = Attacher::AttachEngine3D
  Height = 7
  Length = 4
  Placement = pos=(-1,24.4,0) rot=(0,0,1;0rad)
  Width = 1
FEATURE [Part::Box] Box103  label="Cube087"
  AttacherType = Attacher::AttachEngine3D
  Height = 7
  Length = 4
  Placement = pos=(-1,36.6,0) rot=(0,0,1;0rad)
  Width = 1
FEATURE [Part::Box] Box104  label="Cube088"
  AttacherType = Attacher::AttachEngine3D
  Height = 7
  Length = 4
  Placement = pos=(-1,27.4,0) rot=(0,0,1;0rad)
  Width = 7.2
FEATURE [Part::MultiFuse] Fusion033
  Shapes = -> [Box104,Box101,Box103,Box100,Box102,Box099]
FEATURE [Part::Cut] Cut027
  Base = -> Chamfer009
  Placement = pos=(-5,40,3) rot=(1,0,0;3.14159rad)
  Tool = -> Fusion033
FEATURE [Part::Box] Box105  label="Cube089"
  AttacherType = Attacher::AttachEngine3D
  Height = 10
  Length = 12
  Placement = pos=(-11,-2,-12) rot=(0,0,1;0rad)
  Width = 44
FEATURE [Part::Cut] Cut028
  Base = -> Cut027
  Tool = -> Box105
FEATURE [Part::Box] Box106  label="Cube090"
  AttacherType = Attacher::AttachEngine3D
  Height = 7
  Length = 10
  Placement = pos=(-10,34.6,0) rot=(0,0,1;0rad)
  Width = 2
FEATURE [Part::Box] Box107  label="Cube091"
  AttacherType = Attacher::AttachEngine3D
  Height = 7
  Length = 5
  Width = 40
FEATURE [Part::Box] Box108  label="Cube092"
  AttacherType = Attacher::AttachEngine3D
  Height = 7
  Length = 10
  Placement = pos=(-10,25.4,0) rot=(0,0,1;0rad)
  Width = 2
FEATURE [Part::Box] Box109  label="Cube093"
  AttacherType = Attacher::AttachEngine3D
  Height = 7
  Length = 10
  Placement = pos=(-10,10,0) rot=(0,0,1;0rad)
  Width = 2
FEATURE [Part::Box] Box110  label="Cube094"
  AttacherType = Attacher::AttachEngine3D
  Height = 7
  Length = 10
  Placement = pos=(-10,6,0) rot=(0,0,1;0rad)
  Width = 2
FEATURE [Part::Sphere] Sphere039
  Angle1 = -90
  Angle2 = 90
  Angle3 = 360
  AttacherType = Attacher::AttachEngine3D
  Placement = pos=(-3,6.5,2.5) rot=(0,0,1;0rad)
  Radius = 1.25
FEATURE [Part::Box] Box111  label="Cube095"
  AttacherType = Attacher::AttachEngine3D
  Height = 10
  Length = 13
  Placement = pos=(-10.19,0,-1.19) rot=(0,-1,0;0.785398rad)
  Width = 40
FEATURE [Part::Sphere] Sphere040
  Angle1 = -90
  Angle2 = 90
  Angle3 = 360
  AttacherType = Attacher::AttachEngine3D
  Placement = pos=(-3,11.5,2.5) rot=(0,0,1;0rad)
  Radius = 1.25
FEATURE [Part::Sphere] Sphere041
  Angle1 = -90
  Angle2 = 90
  Angle3 = 360
  AttacherType = Attacher::AttachEngine3D
  Placement = pos=(-3,28,2.5) rot=(0,0,1;0rad)
  Radius = 1.5
FEATURE [Part::Sphere] Sphere042
  Angle1 = -90
  Angle2 = 90
  Angle3 = 360
  AttacherType = Attacher::AttachEngine3D
  Placement = pos=(-3,34,2.5) rot=(0,0,1;0rad)
  Radius = 1.5
FEATURE [Part::MultiFuse] Fusion034
  Shapes = -> [Box107,Box110,Box109,Box108,Box106]
FEATURE [Part::Cut] Cut029
  Base = -> Fusion034
  Tool = -> Box111
FEATURE [Part::MultiFuse] Fusion035
  Shapes = -> [Sphere039,Sphere040,Cut029]
FEATURE [Part::MultiFuse] Fusion036
  Shapes = -> [Sphere042,Sphere041]
FEATURE [Part::Cut] Cut030
  Base = -> Fusion035
  Tool = -> Fusion036
FEATURE [Part::Chamfer] Chamfer010
  Base = -> Cut030
  Edges = 4 edges r=4: [Edge31,Edge37,Edge43,Edge46]
FEATURE [Part::Box] Box112  label="Cube096"
  AttacherType = Attacher::AttachEngine3D
  Height = 7
  Length = 4
  Placement = pos=(-1,5,0) rot=(0,0,1;0rad)
  Width = 1
FEATURE [Part::Box] Box113  label="Cube097"
  AttacherType = Attacher::AttachEngine3D
  Height = 7
  Length = 4
  Placement = pos=(-1,8,0) rot=(0,0,1;0rad)
  Width = 2
FEATURE [Part::Box] Box114  label="Cube098"
  AttacherType = Attacher::AttachEngine3D
  Height = 7
  Length = 4
  Placement = pos=(-1,12,0) rot=(0,0,1;0rad)
  Width = 1
FEATURE [Part::Box] Box115  label="Cube099"
  AttacherType = Attacher::AttachEngine3D
  Height = 7
  Length = 4
  Placement = pos=(-1,24.4,0) rot=(0,0,1;0rad)
  Width = 1
FEATURE [Part::Box] Box116  label="Cube100"
  AttacherType = Attacher::AttachEngine3D
  Height = 7
  Length = 4
  Placement = pos=(-1,36.6,0) rot=(0,0,1;0rad)
  Width = 1
FEATURE [Part::Box] Box117  label="Cube101"
  AttacherType = Attacher::AttachEngine3D
  Height = 7
  Length = 4
  Placement = pos=(-1,27.4,0) rot=(0,0,1;0rad)
  Width = 7.2
FEATURE [Part::MultiFuse] Fusion037
  Shapes = -> [Box117,Box114,Box116,Box113,Box115,Box112]
FEATURE [Part::Cut] Cut031
  Base = -> Chamfer010
  Placement = pos=(-5,40,3) rot=(1,0,0;3.14159rad)
  Tool = -> Fusion037
FEATURE [Part::Box] Box118  label="Cube102"
  AttacherType = Attacher::AttachEngine3D
  Height = 10
  Length = 12
  Placement = pos=(-11,-2,-12) rot=(0,0,1;0rad)
  Width = 44
FEATURE [Part::Cut] Cut032
  Base = -> Cut031
  Placement = pos=(40,0,0) rot=(0,0,1;1.5708rad)
  Tool = -> Box118
FEATURE [Part::Box] Box119  label="Cube103"
  AttacherType = Attacher::AttachEngine3D
  Height = 7
  Length = 4
  Placement = pos=(-1,12,0) rot=(0,0,1;0rad)
  Width = 1
FEATURE [Part::Box] Box120  label="Cube104"
  AttacherType = Attacher::AttachEngine3D
  Height = 10
  Length = 13
  Placement = pos=(-10.19,0,-1.19) rot=(0,-1,0;0.785398rad)
  Width = 40
FEATURE [Part::Box] Box121  label="Cube105"
  AttacherType = Attacher::AttachEngine3D
  Height = 7
  Length = 4
  Placement = pos=(-1,27.4,0) rot=(0,0,1;0rad)
  Width = 7.2
FEATURE [Part::Box] Box122  label="Cube106"
  AttacherType = Attacher::AttachEngine3D
  Height = 7
  Length = 4
  Placement = pos=(-1,5,0) rot=(0,0,1;0rad)
  Width = 1
FEATURE [Part::Box] Box123  label="Cube107"
  AttacherType = Attacher::AttachEngine3D
  Height = 7
  Length = 10
  Placement = pos=(-10,6,0) rot=(0,0,1;0rad)
  Width = 2
FEATURE [Part::Box] Box124  label="Cube108"
  AttacherType = Attacher::AttachEngine3D
  Height = 10
  Length = 12
  Placement = pos=(-11,-2,-12) rot=(0,0,1;0rad)
  Width = 44
FEATURE [Part::Sphere] Sphere043
  Angle1 = -90
  Angle2 = 90
  Angle3 = 360
  AttacherType = Attacher::AttachEngine3D
  Placement = pos=(-3,6.5,2.5) rot=(0,0,1;0rad)
  Radius = 1.25
FEATURE [Part::Box] Box125  label="Cube109"
  AttacherType = Attacher::AttachEngine3D
  Height = 7
  Length = 10
  Placement = pos=(-10,25.4,0) rot=(0,0,1;0rad)
  Width = 2
FEATURE [Part::Box] Box126  label="Cube110"
  AttacherType = Attacher::AttachEngine3D
  Height = 7
  Length = 10
  Placement = pos=(-10,10,0) rot=(0,0,1;0rad)
  Width = 2
FEATURE [Part::Sphere] Sphere044
  Angle1 = -90
  Angle2 = 90
  Angle3 = 360
  AttacherType = Attacher::AttachEngine3D
  Placement = pos=(-3,28,2.5) rot=(0,0,1;0rad)
  Radius = 1.5
FEATURE [Part::Sphere] Sphere045
  Angle1 = -90
  Angle2 = 90
  Angle3 = 360
  AttacherType = Attacher::AttachEngine3D
  Placement = pos=(-3,11.5,2.5) rot=(0,0,1;0rad)
  Radius = 1.25
FEATURE [Part::Box] Box127  label="Cube111"
  AttacherType = Attacher::AttachEngine3D
  Height = 7
  Length = 4
  Placement = pos=(-1,36.6,0) rot=(0,0,1;0rad)
  Width = 1
FEATURE [Part::Sphere] Sphere046
  Angle1 = -90
  Angle2 = 90
  Angle3 = 360
  AttacherType = Attacher::AttachEngine3D
  Placement = pos=(-3,34,2.5) rot=(0,0,1;0rad)
  Radius = 1.5
FEATURE [Part::MultiFuse] Fusion040
  Shapes = -> [Sphere046,Sphere044]
FEATURE [Part::Box] Box128  label="Cube112"
  AttacherType = Attacher::AttachEngine3D
  Height = 7
  Length = 4
  Placement = pos=(-1,8,0) rot=(0,0,1;0rad)
  Width = 2
FEATURE [Part::Box] Box129  label="Cube113"
  AttacherType = Attacher::AttachEngine3D
  Height = 7
  Length = 10
  Placement = pos=(-10,34.6,0) rot=(0,0,1;0rad)
  Width = 2
FEATURE [Part::Box] Box130  label="Cube114"
  AttacherType = Attacher::AttachEngine3D
  Height = 7
  Length = 4
  Placement = pos=(-1,24.4,0) rot=(0,0,1;0rad)
  Width = 1
FEATURE [Part::MultiFuse] Fusion038
  Shapes = -> [Box121,Box119,Box127,Box128,Box130,Box122]
FEATURE [Part::Box] Box131  label="Cube115"
  AttacherType = Attacher::AttachEngine3D
  Height = 7
  Length = 5
  Width = 40
FEATURE [Part::MultiFuse] Fusion041
  Shapes = -> [Box131,Box123,Box126,Box125,Box129]
FEATURE [Part::Cut] Cut035
  Base = -> Fusion041
  Tool = -> Box120
FEATURE [Part::MultiFuse] Fusion039
  Shapes = -> [Sphere043,Sphere045,Cut035]
FEATURE [Part::Cut] Cut036
  Base = -> Fusion039
  Tool = -> Fusion040
FEATURE [Part::Chamfer] Chamfer011
  Base = -> Cut036
  Edges = 4 edges r=4: [Edge31,Edge37,Edge43,Edge46]
FEATURE [Part::Cut] Cut034
  Base = -> Chamfer011
  Placement = pos=(-5,40,3) rot=(1,0,0;3.14159rad)
  Tool = -> Fusion038
FEATURE [Part::Cut] Cut033
  Base = -> Cut034
  Placement = pos=(40,40,0) rot=(0,0,1;3.14159rad)
  Tool = -> Box124
FEATURE [Part::Sphere] Sphere047
  Angle1 = -90
  Angle2 = 90
  Angle3 = 360
  AttacherType = Attacher::AttachEngine3D
  Placement = pos=(-3,11.5,2.5) rot=(0,0,1;0rad)
  Radius = 1.25
FEATURE [Part::Box] Box132  label="Cube116"
  AttacherType = Attacher::AttachEngine3D
  Height = 7
  Length = 10
  Placement = pos=(-10,6,0) rot=(0,0,1;0rad)
  Width = 2
FEATURE [Part::Box] Box133  label="Cube117"
  AttacherType = Attacher::AttachEngine3D
  Height = 7
  Length = 4
  Placement = pos=(-1,8,0) rot=(0,0,1;0rad)
  Width = 2
FEATURE [Part::Box] Box134  label="Cube118"
  AttacherType = Attacher::AttachEngine3D
  Height = 7
  Length = 10
  Placement = pos=(-10,10,0) rot=(0,0,1;0rad)
  Width = 2
FEATURE [Part::Box] Box135  label="Cube119"
  AttacherType = Attacher::AttachEngine3D
  Height = 10
  Length = 12
  Placement = pos=(-11,-2,-12) rot=(0,0,1;0rad)
  Width = 44
FEATURE [Part::Box] Box136  label="Cube120"
  AttacherType = Attacher::AttachEngine3D
  Height = 7
  Length = 4
  Placement = pos=(-1,5,0) rot=(0,0,1;0rad)
  Width = 1
FEATURE [Part::Sphere] Sphere048
  Angle1 = -90
  Angle2 = 90
  Angle3 = 360
  AttacherType = Attacher::AttachEngine3D
  Placement = pos=(-3,28,2.5) rot=(0,0,1;0rad)
  Radius = 1.5
FEATURE [Part::Sphere] Sphere049
  Angle1 = -90
  Angle2 = 90
  Angle3 = 360
  AttacherType = Attacher::AttachEngine3D
  Placement = pos=(-3,6.5,2.5) rot=(0,0,1;0rad)
  Radius = 1.25
FEATURE [Part::Sphere] Sphere050
  Angle1 = -90
  Angle2 = 90
  Angle3 = 360
  AttacherType = Attacher::AttachEngine3D
  Placement = pos=(-3,34,2.5) rot=(0,0,1;0rad)
  Radius = 1.5
FEATURE [Part::Box] Box137  label="Cube121"
  AttacherType = Attacher::AttachEngine3D
  Height = 7
  Length = 4
  Placement = pos=(-1,12,0) rot=(0,0,1;0rad)
  Width = 1
FEATURE [Part::Box] Box138  label="Cube122"
  AttacherType = Attacher::AttachEngine3D
  Height = 7
  Length = 5
  Width = 40
FEATURE [Part::Box] Box139  label="Cube123"
  AttacherType = Attacher::AttachEngine3D
  Height = 7
  Length = 4
  Placement = pos=(-1,36.6,0) rot=(0,0,1;0rad)
  Width = 1
FEATURE [Part::Box] Box140  label="Cube124"
  AttacherType = Attacher::AttachEngine3D
  Height = 7
  Length = 4
  Placement = pos=(-1,24.4,0) rot=(0,0,1;0rad)
  Width = 1
FEATURE [Part::Box] Box141  label="Cube125"
  AttacherType = Attacher::AttachEngine3D
  Height = 7
  Length = 10
  Placement = pos=(-10,25.4,0) rot=(0,0,1;0rad)
  Width = 2
FEATURE [Part::Box] Box142  label="Cube126"
  AttacherType = Attacher::AttachEngine3D
  Height = 10
  Length = 13
  Placement = pos=(-10.19,0,-1.19) rot=(0,-1,0;0.785398rad)
  Width = 40
FEATURE [Part::Box] Box143  label="Cube127"
  AttacherType = Attacher::AttachEngine3D
  Height = 7
  Length = 10
  Placement = pos=(-10,34.6,0) rot=(0,0,1;0rad)
  Width = 2
FEATURE [Part::MultiFuse] Fusion044
  Shapes = -> [Box138,Box132,Box134,Box141,Box143]
FEATURE [Part::Cut] Cut037
  Base = -> Fusion044
  Tool = -> Box142
FEATURE [Part::MultiFuse] Fusion042
  Shapes = -> [Sphere049,Sphere047,Cut037]
FEATURE [Part::MultiFuse] Fusion045
  Shapes = -> [Sphere050,Sphere048]
FEATURE [Part::Cut] Cut038
  Base = -> Fusion042
  Tool = -> Fusion045
FEATURE [Part::Chamfer] Chamfer012
  Base = -> Cut038
  Edges = 4 edges r=4: [Edge31,Edge37,Edge43,Edge46]
FEATURE [Part::Box] Box144  label="Cube128"
  AttacherType = Attacher::AttachEngine3D
  Height = 7
  Length = 4
  Placement = pos=(-1,27.4,0) rot=(0,0,1;0rad)
  Width = 7.2
FEATURE [Part::MultiFuse] Fusion043
  Shapes = -> [Box144,Box137,Box139,Box133,Box140,Box136]
FEATURE [Part::Cut] Cut040
  Base = -> Chamfer012
  Placement = pos=(-5,40,3) rot=(1,0,0;3.14159rad)
  Tool = -> Fusion043
FEATURE [Part::Cut] Cut039
  Base = -> Cut040
  Placement = pos=(0,40,0) rot=(0,0,-1;1.5708rad)
  Tool = -> Box135
FEATURE [Part::MultiFuse] Fusion047
  Placement = pos=(0,40,6.7) rot=(1,0,0;3.14159rad)
  Shapes = -> [Fusion026,Fusion024,Fusion025]
FEATURE [Part::MultiFuse] Fusion048
  Shapes = -> [Box089,Box091,Box090,Box092]
FEATURE [Part::Box] Box145  label="Cube129"
  AttacherType = Attacher::AttachEngine3D
  Height = 15
  Length = 16
  Placement = pos=(12,12,-13) rot=(0,0,1;0rad)
  Width = 16
FEATURE [Part::Box] Box146  label="Cube130"
  AttacherType = Attacher::AttachEngine3D
  Height = 15
  Length = 16.5
  Placement = pos=(11.75,11.75,-3) rot=(0,0,1;0rad)
  Width = 16.5
FEATURE [Part::Chamfer] Chamfer013
  Base = -> Box146
  Edges = 4 edges r=4: [Edge1,Edge3,Edge5,Edge7]
FEATURE [Part::Box] Box147  label="Cube131"
  AttacherType = Attacher::AttachEngine3D
  Height = 10
  Length = 21
  Placement = pos=(9.5,9.5,2.1) rot=(0,0,1;0rad)
  Width = 21
FEATURE [Part::Box] Box148  label="Cube132"
  AttacherType = Attacher::AttachEngine3D
  Height = 14
  Length = 17
  Placement = pos=(11.5,11.5,0) rot=(0,0,1;0rad)
  Width = 17
FEATURE [Part::Cut] Cut043
  Base = -> Box147
  Tool = -> Box148
FEATURE [Part::Chamfer] Chamfer014
  Base = -> Cut043
  Edges = 8 edges r=0.95: [Edge4,Edge5,Edge14,Edge16,Edge17,Edge18,Edge19,Edge20]
FEATURE [Part::Cut] Cut047
  Base = -> Cut003
  Tool = -> Chamfer007
FEATURE [Part::Cut] Cut048
  Base = -> Cut047
  Tool = -> Chamfer008
FEATURE [Part::Cut] Cut049  label="Centre Block"
  Base = -> Cut048
  Tool = -> Box085
FEATURE [Part::Cylinder] Cylinder024
  Angle = 360
  AttacherType = Attacher::AttachEngine3D
  Height = 10
  Placement = pos=(6,6,-5) rot=(0,0,1;0rad)
  Radius = 1.7
FEATURE [Part::Cylinder] Cylinder025
  Angle = 360
  AttacherType = Attacher::AttachEngine3D
  Height = 10
  Placement = pos=(34,20,-5) rot=(0,0,1;0rad)
  Radius = 1.7
FEATURE [Part::Cylinder] Cylinder026
  Angle = 360
  AttacherType = Attacher::AttachEngine3D
  Height = 10
  Placement = pos=(6,34,-5) rot=(0,0,1;0rad)
  Radius = 1.7
FEATURE [Part::MultiFuse] Fusion052  label="Screw Holes to remove ball mags"
  Shapes = -> [Cylinder024,Cylinder025,Cylinder026]
FEATURE [Drawing::FeatureViewAnnotation] Annotation
  Font = Sans
  Rotation = 0
  Scale = 7
  Text = 0.4Added in Holes to Mag plate for removal of magnet
  ViewResult = <g transform="translate(14,23) rotate(0)">\n<text id="Annotation"\n font-family="Sans"\n font-size="7"\n fill="#000000">\n<tspan x="0" dy="1em">0.4Added in Holes to Mag plate for removal of magnet</tspan>\n</text>\n</g>
  Visible = false
  X = 14
  Y = 23
FEATURE [Part::Box] Box149  label="Re-level Edge Clip Block001"
  AttacherType = Attacher::AttachEngine3D
  Height = 10
  Length = 12
  Placement = pos=(-21.5,-2,-7) rot=(0,0,1;0rad)
  Width = 44
FEATURE [Part::Fuse] Fusion  label="Bumps"
  Base = -> Sphere008
  Tool = -> Sphere009
FEATURE [Part::Fuse] Fusion053  label="Holes"
  Base = -> Sphere010
  Tool = -> Sphere011
FEATURE [Part::MultiFuse] Fusion054
  Shapes = -> [Box001,Box002,Box003,Box004,Box005]
FEATURE [Part::Fuse] Fusion055
  Base = -> Fusion
  Tool = -> Fusion054
FEATURE [Part::Cut] Cut
  Base = -> Fusion055
  Tool = -> Fusion053
FEATURE [Part::Cut] Cut056
  Base = -> Cut
  Tool = -> Fusion003
FEATURE [Part::Cut] Cut057
  Base = -> Cut056
  Tool = -> Box013
FEATURE [Part::Cut] Cut058
  Base = -> Cut057
  Tool = -> Box149
FEATURE [Part::Cut] Cut059  label="Edge Clips Master"
  Base = -> Cut058
  Tool = -> Box006
FEATURE [Part::Box] Box150  label="Cube133"
  AttacherType = Attacher::AttachEngine3D
  Height = 7
  Length = 5
  Placement = pos=(-5,0,-2) rot=(0,0,1;0rad)
  Width = 40
FEATURE [Part::Box] Box151  label="Cube134"
  AttacherType = Attacher::AttachEngine3D
  Height = 7
  Length = 10
  Placement = pos=(-15,6,-2) rot=(0,0,1;0rad)
  Width = 2
FEATURE [Part::Box] Box152  label="Cube135"
  AttacherType = Attacher::AttachEngine3D
  Height = 7
  Length = 10
  Placement = pos=(-15,10,-2) rot=(0,0,1;0rad)
  Width = 2
FEATURE [Part::Box] Box153  label="Cube136"
  AttacherType = Attacher::AttachEngine3D
  Height = 7
  Length = 10
  Placement = pos=(-15,25.4,-2) rot=(0,0,1;0rad)
  Width = 2
FEATURE [Part::Box] Box154  label="Cube137"
  AttacherType = Attacher::AttachEngine3D
  Height = 7
  Length = 10
  Placement = pos=(-15,34.6,-2) rot=(0,0,1;0rad)
  Width = 2
FEATURE [Part::Sphere] Sphere051
  Angle1 = -90
  Angle2 = 90
  Angle3 = 360
  AttacherType = Attacher::AttachEngine3D
  Placement = pos=(-7.5,6.5,0.5) rot=(0,0,1;0rad)
  Radius = 1.25
FEATURE [Part::Box] Box155  label="Chamfer Cube001"
  AttacherType = Attacher::AttachEngine3D
  Height = 10
  Length = 13
  Placement = pos=(-11.69,0,-1.19) rot=(0,-1,0;0.785398rad)
  Width = 40
FEATURE [Part::Sphere] Sphere052
  Angle1 = -90
  Angle2 = 90
  Angle3 = 360
  AttacherType = Attacher::AttachEngine3D
  Placement = pos=(-7.5,11.5,0.5) rot=(0,0,1;0rad)
  Radius = 1.25
FEATURE [Part::Sphere] Sphere053
  Angle1 = -90
  Angle2 = 90
  Angle3 = 360
  AttacherType = Attacher::AttachEngine3D
  Placement = pos=(-7.5,28,0.5) rot=(0,0,1;0rad)
  Radius = 1.5
FEATURE [Part::Sphere] Sphere054
  Angle1 = -90
  Angle2 = 90
  Angle3 = 360
  AttacherType = Attacher::AttachEngine3D
  Placement = pos=(-7.5,34,0.5) rot=(0,0,1;0rad)
  Radius = 1.5
FEATURE [Part::Box] Box156  label="Cube138"
  AttacherType = Attacher::AttachEngine3D
  Height = 7
  Length = 4
  Placement = pos=(-6,5,-2) rot=(0,0,1;0rad)
  Width = 1
FEATURE [Part::Box] Box157  label="Cube139"
  AttacherType = Attacher::AttachEngine3D
  Height = 7
  Length = 4
  Placement = pos=(-6,8,-2) rot=(0,0,1;0rad)
  Width = 2
FEATURE [Part::Box] Box158  label="Cube140"
  AttacherType = Attacher::AttachEngine3D
  Height = 7
  Length = 4
  Placement = pos=(-6,12,-2) rot=(0,0,1;0rad)
  Width = 1
FEATURE [Part::Box] Box159  label="Cube141"
  AttacherType = Attacher::AttachEngine3D
  Height = 7
  Length = 4
  Placement = pos=(-6,24.4,-2) rot=(0,0,1;0rad)
  Width = 1
FEATURE [Part::Box] Box160  label="Cube142"
  AttacherType = Attacher::AttachEngine3D
  Height = 7
  Length = 4
  Placement = pos=(-6,36.6,-2) rot=(0,0,1;0rad)
  Width = 1
FEATURE [Part::Box] Box161  label="Cube143"
  AttacherType = Attacher::AttachEngine3D
  Height = 7
  Length = 4
  Placement = pos=(-6,27.4,-2) rot=(0,0,1;0rad)
  Width = 7.2
FEATURE [Part::MultiFuse] Fusion056  label="Extra Holes for Clips001"
  Shapes = -> [Box161,Box158,Box160,Box157,Box159,Box156]
FEATURE [Part::Box] Box162  label="Re-level Edge Clip Block002"
  AttacherType = Attacher::AttachEngine3D
  Height = 10
  Length = 20
  Placement = pos=(-19,-2,3) rot=(0,0,1;0rad)
  Width = 44
FEATURE [Part::Box] Box163  label="Re-level Edge Clip Block003"
  AttacherType = Attacher::AttachEngine3D
  Height = 10
  Length = 12
  Placement = pos=(-21.5,-2,-7) rot=(0,0,1;0rad)
  Width = 44
FEATURE [Part::Fuse] Fusion057  label="Bumps001"
  Base = -> Sphere051
  Tool = -> Sphere052
FEATURE [Part::Fuse] Fusion058  label="Holes001"
  Base = -> Sphere053
  Tool = -> Sphere054
FEATURE [Part::MultiFuse] Fusion059
  Shapes = -> [Box150,Box151,Box152,Box153,Box154]
FEATURE [Part::Fuse] Fusion060
  Base = -> Fusion057
  Tool = -> Fusion059
FEATURE [Part::Cut] Cut060
  Base = -> Fusion060
  Tool = -> Fusion058
FEATURE [Part::Cut] Cut061
  Base = -> Cut060
  Tool = -> Fusion056
FEATURE [Part::Cut] Cut062
  Base = -> Cut061
  Tool = -> Box162
FEATURE [Part::Cut] Cut063
  Base = -> Cut062
  Tool = -> Box163
FEATURE [Part::Cut] Cut064  label="Copy Edge Clips"
  Base = -> Cut063
  Placement = pos=(-7,40,-7) rot=(0.707107,0,-0.707107;3.14159rad)
  Tool = -> Box155
FEATURE [App::DocumentObjectGroup] Group001  label="Old"
  Group = -> [Cut008,Cut009,Cut015,Cut018,Fusion021,Fusion023,Group,Cut039,Cut028,Cut032,Cut033,Fusion048]
FEATURE [Part::Box] Box164  label="Cube144"
  AttacherType = Attacher::AttachEngine3D
  Height = 7
  Length = 5
  Placement = pos=(-5,0,-2) rot=(0,0,1;0rad)
  Width = 40
FEATURE [Part::Box] Box165  label="Cube145"
  AttacherType = Attacher::AttachEngine3D
  Height = 7
  Length = 10
  Placement = pos=(-15,6,-2) rot=(0,0,1;0rad)
  Width = 2
FEATURE [Part::Box] Box166  label="Cube146"
  AttacherType = Attacher::AttachEngine3D
  Height = 7
  Length = 10
  Placement = pos=(-15,10,-2) rot=(0,0,1;0rad)
  Width = 2
FEATURE [Part::Box] Box167  label="Cube147"
  AttacherType = Attacher::AttachEngine3D
  Height = 7
  Length = 10
  Placement = pos=(-15,25.4,-2) rot=(0,0,1;0rad)
  Width = 2
FEATURE [Part::Box] Box168  label="Cube148"
  AttacherType = Attacher::AttachEngine3D
  Height = 7
  Length = 10
  Placement = pos=(-15,34.6,-2) rot=(0,0,1;0rad)
  Width = 2
FEATURE [Part::Sphere] Sphere055
  Angle1 = -90
  Angle2 = 90
  Angle3 = 360
  AttacherType = Attacher::AttachEngine3D
  Placement = pos=(-7.5,6.5,0.5) rot=(0,0,1;0rad)
  Radius = 1.25
FEATURE [Part::Box] Box169  label="Chamfer Cube002"
  AttacherType = Attacher::AttachEngine3D
  Height = 10
  Length = 13
  Placement = pos=(-11.69,0,-1.19) rot=(0,-1,0;0.785398rad)
  Width = 40
FEATURE [Part::Sphere] Sphere056
  Angle1 = -90
  Angle2 = 90
  Angle3 = 360
  AttacherType = Attacher::AttachEngine3D
  Placement = pos=(-7.5,11.5,0.5) rot=(0,0,1;0rad)
  Radius = 1.25
FEATURE [Part::Sphere] Sphere057
  Angle1 = -90
  Angle2 = 90
  Angle3 = 360
  AttacherType = Attacher::AttachEngine3D
  Placement = pos=(-7.5,28,0.5) rot=(0,0,1;0rad)
  Radius = 1.5
FEATURE [Part::Sphere] Sphere058
  Angle1 = -90
  Angle2 = 90
  Angle3 = 360
  AttacherType = Attacher::AttachEngine3D
  Placement = pos=(-7.5,34,0.5) rot=(0,0,1;0rad)
  Radius = 1.5
FEATURE [Part::Box] Box170  label="Cube149"
  AttacherType = Attacher::AttachEngine3D
  Height = 7
  Length = 4
  Placement = pos=(-6,5,-2) rot=(0,0,1;0rad)
  Width = 1
FEATURE [Part::Box] Box171  label="Cube150"
  AttacherType = Attacher::AttachEngine3D
  Height = 7
  Length = 4
  Placement = pos=(-6,8,-2) rot=(0,0,1;0rad)
  Width = 2
FEATURE [Part::Box] Box172  label="Cube151"
  AttacherType = Attacher::AttachEngine3D
  Height = 7
  Length = 4
  Placement = pos=(-6,12,-2) rot=(0,0,1;0rad)
  Width = 1
FEATURE [Part::Box] Box173  label="Cube152"
  AttacherType = Attacher::AttachEngine3D
  Height = 7
  Length = 4
  Placement = pos=(-6,24.4,-2) rot=(0,0,1;0rad)
  Width = 1
FEATURE [Part::Box] Box174  label="Cube153"
  AttacherType = Attacher::AttachEngine3D
  Height = 7
  Length = 4
  Placement = pos=(-6,36.6,-2) rot=(0,0,1;0rad)
  Width = 1
FEATURE [Part::Box] Box175  label="Cube154"
  AttacherType = Attacher::AttachEngine3D
  Height = 7
  Length = 4
  Placement = pos=(-6,27.4,-2) rot=(0,0,1;0rad)
  Width = 7.2
FEATURE [Part::MultiFuse] Fusion061  label="Extra Holes for Clips002"
  Shapes = -> [Box175,Box172,Box174,Box171,Box173,Box170]
FEATURE [Part::Box] Box176  label="Re-level Edge Clip Block004"
  AttacherType = Attacher::AttachEngine3D
  Height = 10
  Length = 20
  Placement = pos=(-19,-2,3) rot=(0,0,1;0rad)
  Width = 44
FEATURE [Part::Box] Box177  label="Re-level Edge Clip Block005"
  AttacherType = Attacher::AttachEngine3D
  Height = 10
  Length = 12
  Placement = pos=(-21.5,-2,-7) rot=(0,0,1;0rad)
  Width = 44
FEATURE [Part::Fuse] Fusion062  label="Bumps002"
  Base = -> Sphere055
  Tool = -> Sphere056
FEATURE [Part::Fuse] Fusion063  label="Holes002"
  Base = -> Sphere057
  Tool = -> Sphere058
FEATURE [Part::MultiFuse] Fusion064
  Shapes = -> [Box164,Box165,Box166,Box167,Box168]
FEATURE [Part::Fuse] Fusion065
  Base = -> Fusion062
  Tool = -> Fusion064
FEATURE [Part::Cut] Cut065
  Base = -> Fusion065
  Tool = -> Fusion063
FEATURE [Part::Cut] Cut066
  Base = -> Cut065
  Tool = -> Fusion061
FEATURE [Part::Cut] Cut067
  Base = -> Cut066
  Tool = -> Box176
FEATURE [Part::Cut] Cut068
  Base = -> Cut067
  Tool = -> Box177
FEATURE [Part::Cut] Cut069  label="Edge Clips001"
  Base = -> Cut068
  Placement = pos=(40,0,0) rot=(0,0,1;1.5708rad)
  Tool = -> Box169
FEATURE [Part::Box] Box178  label="Cube155"
  AttacherType = Attacher::AttachEngine3D
  Height = 7
  Length = 5
  Placement = pos=(-5,0,-2) rot=(0,0,1;0rad)
  Width = 40
FEATURE [Part::Box] Box179  label="Cube156"
  AttacherType = Attacher::AttachEngine3D
  Height = 7
  Length = 10
  Placement = pos=(-15,10,-2) rot=(0,0,1;0rad)
  Width = 2
FEATURE [Part::Box] Box180  label="Re-level Edge Clip Block006"
  AttacherType = Attacher::AttachEngine3D
  Height = 10
  Length = 20
  Placement = pos=(-19,-2,3) rot=(0,0,1;0rad)
  Width = 44
FEATURE [Part::Box] Box181  label="Cube157"
  AttacherType = Attacher::AttachEngine3D
  Height = 7
  Length = 4
  Placement = pos=(-6,27.4,-2) rot=(0,0,1;0rad)
  Width = 7.2
FEATURE [Part::Box] Box182  label="Cube158"
  AttacherType = Attacher::AttachEngine3D
  Height = 7
  Length = 4
  Placement = pos=(-6,12,-2) rot=(0,0,1;0rad)
  Width = 1
FEATURE [Part::Sphere] Sphere059
  Angle1 = -90
  Angle2 = 90
  Angle3 = 360
  AttacherType = Attacher::AttachEngine3D
  Placement = pos=(-7.5,6.5,0.5) rot=(0,0,1;0rad)
  Radius = 1.25
FEATURE [Part::Box] Box183  label="Cube159"
  AttacherType = Attacher::AttachEngine3D
  Height = 7
  Length = 10
  Placement = pos=(-15,25.4,-2) rot=(0,0,1;0rad)
  Width = 2
FEATURE [Part::Box] Box184  label="Cube160"
  AttacherType = Attacher::AttachEngine3D
  Height = 7
  Length = 4
  Placement = pos=(-6,36.6,-2) rot=(0,0,1;0rad)
  Width = 1
FEATURE [Part::Sphere] Sphere060
  Angle1 = -90
  Angle2 = 90
  Angle3 = 360
  AttacherType = Attacher::AttachEngine3D
  Placement = pos=(-7.5,34,0.5) rot=(0,0,1;0rad)
  Radius = 1.5
FEATURE [Part::Box] Box185  label="Cube161"
  AttacherType = Attacher::AttachEngine3D
  Height = 7
  Length = 4
  Placement = pos=(-6,24.4,-2) rot=(0,0,1;0rad)
  Width = 1
FEATURE [Part::Box] Box186  label="Cube162"
  AttacherType = Attacher::AttachEngine3D
  Height = 7
  Length = 4
  Placement = pos=(-6,8,-2) rot=(0,0,1;0rad)
  Width = 2
FEATURE [Part::Box] Box187  label="Re-level Edge Clip Block007"
  AttacherType = Attacher::AttachEngine3D
  Height = 10
  Length = 12
  Placement = pos=(-21.5,-2,-7) rot=(0,0,1;0rad)
  Width = 44
FEATURE [Part::Sphere] Sphere061
  Angle1 = -90
  Angle2 = 90
  Angle3 = 360
  AttacherType = Attacher::AttachEngine3D
  Placement = pos=(-7.5,11.5,0.5) rot=(0,0,1;0rad)
  Radius = 1.25
FEATURE [Part::Sphere] Sphere062
  Angle1 = -90
  Angle2 = 90
  Angle3 = 360
  AttacherType = Attacher::AttachEngine3D
  Placement = pos=(-7.5,28,0.5) rot=(0,0,1;0rad)
  Radius = 1.5
FEATURE [Part::Fuse] Fusion066  label="Holes003"
  Base = -> Sphere062
  Tool = -> Sphere060
FEATURE [Part::Box] Box188  label="Cube163"
  AttacherType = Attacher::AttachEngine3D
  Height = 7
  Length = 10
  Placement = pos=(-15,34.6,-2) rot=(0,0,1;0rad)
  Width = 2
FEATURE [Part::Box] Box189  label="Cube164"
  AttacherType = Attacher::AttachEngine3D
  Height = 7
  Length = 4
  Placement = pos=(-6,5,-2) rot=(0,0,1;0rad)
  Width = 1
FEATURE [Part::MultiFuse] Fusion067  label="Extra Holes for Clips003"
  Shapes = -> [Box181,Box182,Box184,Box186,Box185,Box189]
FEATURE [Part::Box] Box190  label="Cube165"
  AttacherType = Attacher::AttachEngine3D
  Height = 7
  Length = 10
  Placement = pos=(-15,6,-2) rot=(0,0,1;0rad)
  Width = 2
FEATURE [Part::MultiFuse] Fusion069
  Shapes = -> [Box178,Box190,Box179,Box183,Box188]
FEATURE [Part::Fuse] Fusion070  label="Bumps003"
  Base = -> Sphere059
  Tool = -> Sphere061
FEATURE [Part::Fuse] Fusion068
  Base = -> Fusion070
  Tool = -> Fusion069
FEATURE [Part::Cut] Cut073
  Base = -> Fusion068
  Tool = -> Fusion066
FEATURE [Part::Cut] Cut070
  Base = -> Cut073
  Tool = -> Fusion067
FEATURE [Part::Cut] Cut071
  Base = -> Cut070
  Tool = -> Box180
FEATURE [Part::Cut] Cut072
  Base = -> Cut071
  Tool = -> Box187
FEATURE [Part::Box] Box191  label="Chamfer Cube003"
  AttacherType = Attacher::AttachEngine3D
  Height = 10
  Length = 13
  Placement = pos=(-11.69,0,-1.19) rot=(0,-1,0;0.785398rad)
  Width = 40
FEATURE [Part::Cut] Cut074  label="Edge Clips002"
  Base = -> Cut072
  Placement = pos=(40,40,0) rot=(0,0,1;3.14159rad)
  Tool = -> Box191
FEATURE [Part::Box] Box192  label="Cube166"
  AttacherType = Attacher::AttachEngine3D
  Height = 7
  Length = 10
  Placement = pos=(-15,6,-2) rot=(0,0,1;0rad)
  Width = 2
FEATURE [Part::Box] Box193  label="Chamfer Cube004"
  AttacherType = Attacher::AttachEngine3D
  Height = 10
  Length = 13
  Placement = pos=(-11.69,0,-1.19) rot=(0,-1,0;0.785398rad)
  Width = 40
FEATURE [Part::Box] Box194  label="Re-level Edge Clip Block008"
  AttacherType = Attacher::AttachEngine3D
  Height = 10
  Length = 20
  Placement = pos=(-19,-2,3) rot=(0,0,1;0rad)
  Width = 44
FEATURE [Part::Box] Box195  label="Cube167"
  AttacherType = Attacher::AttachEngine3D
  Height = 7
  Length = 10
  Placement = pos=(-15,10,-2) rot=(0,0,1;0rad)
  Width = 2
FEATURE [Part::Box] Box196  label="Cube168"
  AttacherType = Attacher::AttachEngine3D
  Height = 7
  Length = 5
  Placement = pos=(-5,0,-2) rot=(0,0,1;0rad)
  Width = 40
FEATURE [Part::Box] Box197  label="Cube169"
  AttacherType = Attacher::AttachEngine3D
  Height = 7
  Length = 4
  Placement = pos=(-6,5,-2) rot=(0,0,1;0rad)
  Width = 1
FEATURE [Part::Box] Box198  label="Cube170"
  AttacherType = Attacher::AttachEngine3D
  Height = 7
  Length = 4
  Placement = pos=(-6,12,-2) rot=(0,0,1;0rad)
  Width = 1
FEATURE [Part::Box] Box199  label="Cube171"
  AttacherType = Attacher::AttachEngine3D
  Height = 7
  Length = 4
  Placement = pos=(-6,27.4,-2) rot=(0,0,1;0rad)
  Width = 7.2
FEATURE [Part::Box] Box200  label="Cube172"
  AttacherType = Attacher::AttachEngine3D
  Height = 7
  Length = 4
  Placement = pos=(-6,24.4,-2) rot=(0,0,1;0rad)
  Width = 1
FEATURE [Part::Sphere] Sphere063
  Angle1 = -90
  Angle2 = 90
  Angle3 = 360
  AttacherType = Attacher::AttachEngine3D
  Placement = pos=(-7.5,28,0.5) rot=(0,0,1;0rad)
  Radius = 1.5
FEATURE [Part::Sphere] Sphere064
  Angle1 = -90
  Angle2 = 90
  Angle3 = 360
  AttacherType = Attacher::AttachEngine3D
  Placement = pos=(-7.5,11.5,0.5) rot=(0,0,1;0rad)
  Radius = 1.25
FEATURE [Part::Box] Box201  label="Cube173"
  AttacherType = Attacher::AttachEngine3D
  Height = 7
  Length = 4
  Placement = pos=(-6,8,-2) rot=(0,0,1;0rad)
  Width = 2
FEATURE [Part::Box] Box202  label="Cube174"
  AttacherType = Attacher::AttachEngine3D
  Height = 7
  Length = 10
  Placement = pos=(-15,25.4,-2) rot=(0,0,1;0rad)
  Width = 2
FEATURE [Part::Sphere] Sphere065
  Angle1 = -90
  Angle2 = 90
  Angle3 = 360
  AttacherType = Attacher::AttachEngine3D
  Placement = pos=(-7.5,6.5,0.5) rot=(0,0,1;0rad)
  Radius = 1.25
FEATURE [Part::Fuse] Fusion073  label="Bumps004"
  Base = -> Sphere065
  Tool = -> Sphere064
FEATURE [Part::Sphere] Sphere066
  Angle1 = -90
  Angle2 = 90
  Angle3 = 360
  AttacherType = Attacher::AttachEngine3D
  Placement = pos=(-7.5,34,0.5) rot=(0,0,1;0rad)
  Radius = 1.5
FEATURE [Part::Fuse] Fusion071  label="Holes004"
  Base = -> Sphere063
  Tool = -> Sphere066
FEATURE [Part::Box] Box203  label="Re-level Edge Clip Block009"
  AttacherType = Attacher::AttachEngine3D
  Height = 10
  Length = 12
  Placement = pos=(-21.5,-2,-7) rot=(0,0,1;0rad)
  Width = 44
FEATURE [Part::Box] Box204  label="Cube175"
  AttacherType = Attacher::AttachEngine3D
  Height = 7
  Length = 4
  Placement = pos=(-6,36.6,-2) rot=(0,0,1;0rad)
  Width = 1
FEATURE [Part::MultiFuse] Fusion074  label="Extra Holes for Clips004"
  Shapes = -> [Box199,Box198,Box204,Box201,Box200,Box197]
FEATURE [Part::Box] Box205  label="Cube176"
  AttacherType = Attacher::AttachEngine3D
  Height = 7
  Length = 10
  Placement = pos=(-15,34.6,-2) rot=(0,0,1;0rad)
  Width = 2
FEATURE [Part::MultiFuse] Fusion072
  Shapes = -> [Box196,Box192,Box195,Box202,Box205]
FEATURE [Part::Fuse] Fusion075
  Base = -> Fusion073
  Tool = -> Fusion072
FEATURE [Part::Cut] Cut075
  Base = -> Fusion075
  Tool = -> Fusion071
FEATURE [Part::Cut] Cut076
  Base = -> Cut075
  Tool = -> Fusion074
FEATURE [Part::Cut] Cut078
  Base = -> Cut076
  Tool = -> Box194
FEATURE [Part::Cut] Cut077
  Base = -> Cut078
  Tool = -> Box203
FEATURE [Part::Cut] Cut079  label="Edge Clips003"
  Base = -> Cut077
  Placement = pos=(0,40,0) rot=(0,0,-1;1.5708rad)
  Tool = -> Box193
FEATURE [Part::MultiFuse] Fusion076  label="Edge Clips Fusion"
  Shapes = -> [Cut059,Cut069,Cut074,Cut079]
FEATURE [Part::Cut] Cut080
  Base = -> Cut049
  Tool = -> Fusion052
FEATURE [Part::Fuse] Fusion077
  Base = -> Fusion076
  Tool = -> Cut080
FEATURE [Part::Box] Box206  label="Cube177"
  AttacherType = Attacher::AttachEngine3D
  Height = 10
  Length = 10
  Placement = pos=(46,24,1) rot=(0.442189,-0.287968,0.849437;1.66134rad)
  Width = 15
FEATURE [Part::Box] Box207  label="Cube178"
  AttacherType = Attacher::AttachEngine3D
  Height = 10
  Length = 10
  Placement = pos=(16,46,1) rot=(0.381439,0.080566,0.920876;3.07487rad)
  Width = 15
FEATURE [Part::Box] Box208  label="Cube179"
  AttacherType = Attacher::AttachEngine3D
  Height = 10
  Length = 10
  Placement = pos=(-6,16,1) rot=(-0.273007,-0.419215,-0.865867;1.78566rad)
  Width = 15
FEATURE [Part::MultiFuse] Fusion078  label="Glue Dents"
  Shapes = -> [Box086,Box208,Box207,Box206]
FEATURE [Part::Cut] Cut081  label="Ball Plate"
  Base = -> Fusion077
  Tool = -> Fusion078
FEATURE [Part::Box] Box209  label="Cube180"
  AttacherType = Attacher::AttachEngine3D
  Height = 7
  Length = 5
  Placement = pos=(-5,0,-2) rot=(0,0,1;0rad)
  Width = 40
FEATURE [Part::Box] Box210  label="Cube181"
  AttacherType = Attacher::AttachEngine3D
  Height = 7
  Length = 10
  Placement = pos=(-15,6,-2) rot=(0,0,1;0rad)
  Width = 2
FEATURE [Part::Box] Box211  label="Cube182"
  AttacherType = Attacher::AttachEngine3D
  Height = 7
  Length = 10
  Placement = pos=(-15,10,-2) rot=(0,0,1;0rad)
  Width = 2
FEATURE [Part::Box] Box212  label="Cube183"
  AttacherType = Attacher::AttachEngine3D
  Height = 7
  Length = 10
  Placement = pos=(-15,25.4,-2) rot=(0,0,1;0rad)
  Width = 2
FEATURE [Part::Box] Box213  label="Cube184"
  AttacherType = Attacher::AttachEngine3D
  Height = 7
  Length = 10
  Placement = pos=(-15,34.6,-2) rot=(0,0,1;0rad)
  Width = 2
FEATURE [Part::Sphere] Sphere067
  Angle1 = -90
  Angle2 = 90
  Angle3 = 360
  AttacherType = Attacher::AttachEngine3D
  Placement = pos=(-7.5,6.5,0.5) rot=(0,0,1;0rad)
  Radius = 1.25
FEATURE [Part::Box] Box214  label="Chamfer Cube005"
  AttacherType = Attacher::AttachEngine3D
  Height = 10
  Length = 13
  Placement = pos=(-11.69,0,-1.19) rot=(0,-1,0;0.785398rad)
  Width = 40
FEATURE [Part::Sphere] Sphere068
  Angle1 = -90
  Angle2 = 90
  Angle3 = 360
  AttacherType = Attacher::AttachEngine3D
  Placement = pos=(-7.5,11.5,0.5) rot=(0,0,1;0rad)
  Radius = 1.25
FEATURE [Part::Sphere] Sphere069
  Angle1 = -90
  Angle2 = 90
  Angle3 = 360
  AttacherType = Attacher::AttachEngine3D
  Placement = pos=(-7.5,28,0.5) rot=(0,0,1;0rad)
  Radius = 1.5
FEATURE [Part::Sphere] Sphere070
  Angle1 = -90
  Angle2 = 90
  Angle3 = 360
  AttacherType = Attacher::AttachEngine3D
  Placement = pos=(-7.5,34,0.5) rot=(0,0,1;0rad)
  Radius = 1.5
FEATURE [Part::Box] Box215  label="Cube185"
  AttacherType = Attacher::AttachEngine3D
  Height = 7
  Length = 4
  Placement = pos=(-6,5,-2) rot=(0,0,1;0rad)
  Width = 1
FEATURE [Part::Box] Box216  label="Cube186"
  AttacherType = Attacher::AttachEngine3D
  Height = 7
  Length = 4
  Placement = pos=(-6,8,-2) rot=(0,0,1;0rad)
  Width = 2
FEATURE [Part::Box] Box217  label="Cube187"
  AttacherType = Attacher::AttachEngine3D
  Height = 7
  Length = 4
  Placement = pos=(-6,12,-2) rot=(0,0,1;0rad)
  Width = 1
FEATURE [Part::Box] Box218  label="Cube188"
  AttacherType = Attacher::AttachEngine3D
  Height = 7
  Length = 4
  Placement = pos=(-6,24.4,-2) rot=(0,0,1;0rad)
  Width = 1
FEATURE [Part::Box] Box219  label="Cube189"
  AttacherType = Attacher::AttachEngine3D
  Height = 7
  Length = 4
  Placement = pos=(-6,36.6,-2) rot=(0,0,1;0rad)
  Width = 1
FEATURE [Part::Box] Box220  label="Cube190"
  AttacherType = Attacher::AttachEngine3D
  Height = 7
  Length = 4
  Placement = pos=(-6,27.4,-2) rot=(0,0,1;0rad)
  Width = 7.2
FEATURE [Part::MultiFuse] Fusion079  label="Extra Holes for Clips005"
  Shapes = -> [Box220,Box217,Box219,Box216,Box218,Box215]
FEATURE [Part::Box] Box221  label="Re-level Edge Clip Block010"
  AttacherType = Attacher::AttachEngine3D
  Height = 10
  Length = 20
  Placement = pos=(-19,-2,3) rot=(0,0,1;0rad)
  Width = 44
FEATURE [Part::Box] Box222  label="Re-level Edge Clip Block011"
  AttacherType = Attacher::AttachEngine3D
  Height = 10
  Length = 12
  Placement = pos=(-21.5,-2,-7) rot=(0,0,1;0rad)
  Width = 44
FEATURE [Part::Fuse] Fusion080  label="Bumps005"
  Base = -> Sphere067
  Tool = -> Sphere068
FEATURE [Part::Fuse] Fusion081  label="Holes005"
  Base = -> Sphere069
  Tool = -> Sphere070
FEATURE [Part::MultiFuse] Fusion082
  Shapes = -> [Box209,Box210,Box211,Box212,Box213]
FEATURE [Part::Fuse] Fusion083
  Base = -> Fusion080
  Tool = -> Fusion082
FEATURE [Part::Cut] Cut082
  Base = -> Fusion083
  Tool = -> Fusion081
FEATURE [Part::Cut] Cut083
  Base = -> Cut082
  Tool = -> Fusion079
FEATURE [Part::Cut] Cut084
  Base = -> Cut083
  Tool = -> Box221
FEATURE [Part::Cut] Cut085
  Base = -> Cut084
  Tool = -> Box222
FEATURE [Part::Cut] Cut086  label="Edge Clips Master001"
  Base = -> Cut085
  Tool = -> Box214
FEATURE [Part::Box] Box223  label="Cube191"
  AttacherType = Attacher::AttachEngine3D
  Height = 7
  Length = 5
  Placement = pos=(-5,0,-2) rot=(0,0,1;0rad)
  Width = 40
FEATURE [Part::Box] Box224  label="Cube192"
  AttacherType = Attacher::AttachEngine3D
  Height = 7
  Length = 4
  Placement = pos=(-6,8,-2) rot=(0,0,1;0rad)
  Width = 2
FEATURE [Part::Box] Box225  label="Chamfer Cube006"
  AttacherType = Attacher::AttachEngine3D
  Height = 10
  Length = 13
  Placement = pos=(-11.69,0,-1.19) rot=(0,-1,0;0.785398rad)
  Width = 40
FEATURE [Part::Box] Box226  label="Cube193"
  AttacherType = Attacher::AttachEngine3D
  Height = 7
  Length = 10
  Placement = pos=(-15,6,-2) rot=(0,0,1;0rad)
  Width = 2
FEATURE [Part::Sphere] Sphere071
  Angle1 = -90
  Angle2 = 90
  Angle3 = 360
  AttacherType = Attacher::AttachEngine3D
  Placement = pos=(-7.5,11.5,0.5) rot=(0,0,1;0rad)
  Radius = 1.25
FEATURE [Part::Box] Box227  label="Cube194"
  AttacherType = Attacher::AttachEngine3D
  Height = 7
  Length = 4
  Placement = pos=(-6,27.4,-2) rot=(0,0,1;0rad)
  Width = 7.2
FEATURE [Part::Box] Box228  label="Cube195"
  AttacherType = Attacher::AttachEngine3D
  Height = 7
  Length = 4
  Placement = pos=(-6,12,-2) rot=(0,0,1;0rad)
  Width = 1
FEATURE [Part::Box] Box229  label="Cube196"
  AttacherType = Attacher::AttachEngine3D
  Height = 7
  Length = 4
  Placement = pos=(-6,24.4,-2) rot=(0,0,1;0rad)
  Width = 1
FEATURE [Part::Sphere] Sphere072
  Angle1 = -90
  Angle2 = 90
  Angle3 = 360
  AttacherType = Attacher::AttachEngine3D
  Placement = pos=(-7.5,6.5,0.5) rot=(0,0,1;0rad)
  Radius = 1.25
FEATURE [Part::Box] Box230  label="Cube197"
  AttacherType = Attacher::AttachEngine3D
  Height = 7
  Length = 4
  Placement = pos=(-6,36.6,-2) rot=(0,0,1;0rad)
  Width = 1
FEATURE [Part::Box] Box231  label="Cube198"
  AttacherType = Attacher::AttachEngine3D
  Height = 7
  Length = 10
  Placement = pos=(-15,10,-2) rot=(0,0,1;0rad)
  Width = 2
FEATURE [Part::Sphere] Sphere073
  Angle1 = -90
  Angle2 = 90
  Angle3 = 360
  AttacherType = Attacher::AttachEngine3D
  Placement = pos=(-7.5,34,0.5) rot=(0,0,1;0rad)
  Radius = 1.5
FEATURE [Part::Box] Box232  label="Cube199"
  AttacherType = Attacher::AttachEngine3D
  Height = 7
  Length = 4
  Placement = pos=(-6,5,-2) rot=(0,0,1;0rad)
  Width = 1
FEATURE [Part::MultiFuse] Fusion085  label="Extra Holes for Clips006"
  Shapes = -> [Box227,Box228,Box230,Box224,Box229,Box232]
FEATURE [Part::Box] Box233  label="Re-level Edge Clip Block012"
  AttacherType = Attacher::AttachEngine3D
  Height = 10
  Length = 20
  Placement = pos=(-19,-2,3) rot=(0,0,1;0rad)
  Width = 44
FEATURE [Part::Box] Box234  label="Cube200"
  AttacherType = Attacher::AttachEngine3D
  Height = 7
  Length = 10
  Placement = pos=(-15,34.6,-2) rot=(0,0,1;0rad)
  Width = 2
FEATURE [Part::Box] Box235  label="Cube201"
  AttacherType = Attacher::AttachEngine3D
  Height = 7
  Length = 10
  Placement = pos=(-15,25.4,-2) rot=(0,0,1;0rad)
  Width = 2
FEATURE [Part::MultiFuse] Fusion086
  Shapes = -> [Box223,Box226,Box231,Box235,Box234]
FEATURE [Part::Fuse] Fusion087  label="Bumps006"
  Base = -> Sphere072
  Tool = -> Sphere071
FEATURE [Part::Fuse] Fusion084
  Base = -> Fusion087
  Tool = -> Fusion086
FEATURE [Part::Sphere] Sphere074
  Angle1 = -90
  Angle2 = 90
  Angle3 = 360
  AttacherType = Attacher::AttachEngine3D
  Placement = pos=(-7.5,28,0.5) rot=(0,0,1;0rad)
  Radius = 1.5
FEATURE [Part::Fuse] Fusion088  label="Holes006"
  Base = -> Sphere074
  Tool = -> Sphere073
FEATURE [Part::Box] Box236  label="Re-level Edge Clip Block013"
  AttacherType = Attacher::AttachEngine3D
  Height = 10
  Length = 12
  Placement = pos=(-21.5,-2,-7) rot=(0,0,1;0rad)
  Width = 44
FEATURE [Part::Cut] Cut087
  Base = -> Fusion084
  Tool = -> Fusion088
FEATURE [Part::Cut] Cut088
  Base = -> Cut087
  Tool = -> Fusion085
FEATURE [Part::Cut] Cut089
  Base = -> Cut088
  Tool = -> Box233
FEATURE [Part::Cut] Cut090
  Base = -> Cut089
  Tool = -> Box236
FEATURE [Part::Cut] Cut091  label="Edge Clips004"
  Base = -> Cut090
  Placement = pos=(40,0,0) rot=(0,0,1;1.5708rad)
  Tool = -> Box225
FEATURE [Part::Box] Box237  label="Re-level Edge Clip Block014"
  AttacherType = Attacher::AttachEngine3D
  Height = 10
  Length = 12
  Placement = pos=(-21.5,-2,-7) rot=(0,0,1;0rad)
  Width = 44
FEATURE [Part::Box] Box238  label="Cube202"
  AttacherType = Attacher::AttachEngine3D
  Height = 7
  Length = 4
  Placement = pos=(-6,36.6,-2) rot=(0,0,1;0rad)
  Width = 1
FEATURE [Part::Box] Box239  label="Cube203"
  AttacherType = Attacher::AttachEngine3D
  Height = 7
  Length = 10
  Placement = pos=(-15,10,-2) rot=(0,0,1;0rad)
  Width = 2
FEATURE [Part::Box] Box240  label="Cube204"
  AttacherType = Attacher::AttachEngine3D
  Height = 7
  Length = 10
  Placement = pos=(-15,25.4,-2) rot=(0,0,1;0rad)
  Width = 2
FEATURE [Part::Box] Box241  label="Re-level Edge Clip Block015"
  AttacherType = Attacher::AttachEngine3D
  Height = 10
  Length = 20
  Placement = pos=(-19,-2,3) rot=(0,0,1;0rad)
  Width = 44
FEATURE [Part::Box] Box242  label="Cube205"
  AttacherType = Attacher::AttachEngine3D
  Height = 7
  Length = 10
  Placement = pos=(-15,34.6,-2) rot=(0,0,1;0rad)
  Width = 2
FEATURE [Part::Sphere] Sphere075
  Angle1 = -90
  Angle2 = 90
  Angle3 = 360
  AttacherType = Attacher::AttachEngine3D
  Placement = pos=(-7.5,34,0.5) rot=(0,0,1;0rad)
  Radius = 1.5
FEATURE [Part::Sphere] Sphere076
  Angle1 = -90
  Angle2 = 90
  Angle3 = 360
  AttacherType = Attacher::AttachEngine3D
  Placement = pos=(-7.5,28,0.5) rot=(0,0,1;0rad)
  Radius = 1.5
FEATURE [Part::Fuse] Fusion089  label="Holes007"
  Base = -> Sphere076
  Tool = -> Sphere075
FEATURE [Part::Box] Box243  label="Cube206"
  AttacherType = Attacher::AttachEngine3D
  Height = 7
  Length = 4
  Placement = pos=(-6,5,-2) rot=(0,0,1;0rad)
  Width = 1
FEATURE [Part::Box] Box244  label="Cube207"
  AttacherType = Attacher::AttachEngine3D
  Height = 7
  Length = 4
  Placement = pos=(-6,24.4,-2) rot=(0,0,1;0rad)
  Width = 1
FEATURE [Part::Sphere] Sphere077
  Angle1 = -90
  Angle2 = 90
  Angle3 = 360
  AttacherType = Attacher::AttachEngine3D
  Placement = pos=(-7.5,11.5,0.5) rot=(0,0,1;0rad)
  Radius = 1.25
FEATURE [Part::Box] Box245  label="Cube208"
  AttacherType = Attacher::AttachEngine3D
  Height = 7
  Length = 4
  Placement = pos=(-6,12,-2) rot=(0,0,1;0rad)
  Width = 1
FEATURE [Part::Box] Box246  label="Chamfer Cube007"
  AttacherType = Attacher::AttachEngine3D
  Height = 10
  Length = 13
  Placement = pos=(-11.69,0,-1.19) rot=(0,-1,0;0.785398rad)
  Width = 40
FEATURE [Part::Sphere] Sphere078
  Angle1 = -90
  Angle2 = 90
  Angle3 = 360
  AttacherType = Attacher::AttachEngine3D
  Placement = pos=(-7.5,6.5,0.5) rot=(0,0,1;0rad)
  Radius = 1.25
FEATURE [Part::Fuse] Fusion090  label="Bumps007"
  Base = -> Sphere078
  Tool = -> Sphere077
FEATURE [Part::Box] Box247  label="Cube209"
  AttacherType = Attacher::AttachEngine3D
  Height = 7
  Length = 5
  Placement = pos=(-5,0,-2) rot=(0,0,1;0rad)
  Width = 40
FEATURE [Part::Box] Box248  label="Cube210"
  AttacherType = Attacher::AttachEngine3D
  Height = 7
  Length = 4
  Placement = pos=(-6,27.4,-2) rot=(0,0,1;0rad)
  Width = 7.2
FEATURE [Part::Box] Box249  label="Cube211"
  AttacherType = Attacher::AttachEngine3D
  Height = 7
  Length = 4
  Placement = pos=(-6,8,-2) rot=(0,0,1;0rad)
  Width = 2
FEATURE [Part::MultiFuse] Fusion091  label="Extra Holes for Clips007"
  Shapes = -> [Box248,Box245,Box238,Box249,Box244,Box243]
FEATURE [Part::Box] Box250  label="Cube212"
  AttacherType = Attacher::AttachEngine3D
  Height = 7
  Length = 10
  Placement = pos=(-15,6,-2) rot=(0,0,1;0rad)
  Width = 2
FEATURE [Part::MultiFuse] Fusion092
  Shapes = -> [Box247,Box250,Box239,Box240,Box242]
FEATURE [Part::Fuse] Fusion093
  Base = -> Fusion090
  Tool = -> Fusion092
FEATURE [Part::Cut] Cut093
  Base = -> Fusion093
  Tool = -> Fusion089
FEATURE [Part::Cut] Cut094
  Base = -> Cut093
  Tool = -> Fusion091
FEATURE [Part::Cut] Cut095
  Base = -> Cut094
  Tool = -> Box241
FEATURE [Part::Cut] Cut096
  Base = -> Cut095
  Tool = -> Box237
FEATURE [Part::Cut] Cut092  label="Edge Clips005"
  Base = -> Cut096
  Placement = pos=(40,40,0) rot=(0,0,1;3.14159rad)
  Tool = -> Box246
FEATURE [Part::Box] Box251  label="Re-level Edge Clip Block016"
  AttacherType = Attacher::AttachEngine3D
  Height = 10
  Length = 12
  Placement = pos=(-21.5,-2,-7) rot=(0,0,1;0rad)
  Width = 44
FEATURE [Part::Box] Box252  label="Cube213"
  AttacherType = Attacher::AttachEngine3D
  Height = 7
  Length = 10
  Placement = pos=(-15,10,-2) rot=(0,0,1;0rad)
  Width = 2
FEATURE [Part::Box] Box253  label="Cube214"
  AttacherType = Attacher::AttachEngine3D
  Height = 7
  Length = 4
  Placement = pos=(-6,12,-2) rot=(0,0,1;0rad)
  Width = 1
FEATURE [Part::Box] Box254  label="Chamfer Cube008"
  AttacherType = Attacher::AttachEngine3D
  Height = 10
  Length = 13
  Placement = pos=(-11.69,0,-1.19) rot=(0,-1,0;0.785398rad)
  Width = 40
FEATURE [Part::Sphere] Sphere079
  Angle1 = -90
  Angle2 = 90
  Angle3 = 360
  AttacherType = Attacher::AttachEngine3D
  Placement = pos=(-7.5,6.5,0.5) rot=(0,0,1;0rad)
  Radius = 1.25
FEATURE [Part::Box] Box255  label="Cube215"
  AttacherType = Attacher::AttachEngine3D
  Height = 7
  Length = 5
  Placement = pos=(-5,0,-2) rot=(0,0,1;0rad)
  Width = 40
FEATURE [Part::Box] Box256  label="Cube216"
  AttacherType = Attacher::AttachEngine3D
  Height = 7
  Length = 4
  Placement = pos=(-6,27.4,-2) rot=(0,0,1;0rad)
  Width = 7.2
FEATURE [Part::Box] Box257  label="Cube217"
  AttacherType = Attacher::AttachEngine3D
  Height = 7
  Length = 4
  Placement = pos=(-6,8,-2) rot=(0,0,1;0rad)
  Width = 2
FEATURE [Part::Box] Box258  label="Cube218"
  AttacherType = Attacher::AttachEngine3D
  Height = 7
  Length = 10
  Placement = pos=(-15,6,-2) rot=(0,0,1;0rad)
  Width = 2
FEATURE [Part::Sphere] Sphere080
  Angle1 = -90
  Angle2 = 90
  Angle3 = 360
  AttacherType = Attacher::AttachEngine3D
  Placement = pos=(-7.5,28,0.5) rot=(0,0,1;0rad)
  Radius = 1.5
FEATURE [Part::Box] Box259  label="Cube219"
  AttacherType = Attacher::AttachEngine3D
  Height = 7
  Length = 4
  Placement = pos=(-6,5,-2) rot=(0,0,1;0rad)
  Width = 1
FEATURE [Part::Box] Box260  label="Cube220"
  AttacherType = Attacher::AttachEngine3D
  Height = 7
  Length = 4
  Placement = pos=(-6,24.4,-2) rot=(0,0,1;0rad)
  Width = 1
FEATURE [Part::Sphere] Sphere081
  Angle1 = -90
  Angle2 = 90
  Angle3 = 360
  AttacherType = Attacher::AttachEngine3D
  Placement = pos=(-7.5,11.5,0.5) rot=(0,0,1;0rad)
  Radius = 1.25
FEATURE [Part::Box] Box261  label="Re-level Edge Clip Block017"
  AttacherType = Attacher::AttachEngine3D
  Height = 10
  Length = 20
  Placement = pos=(-19,-2,3) rot=(0,0,1;0rad)
  Width = 44
FEATURE [Part::Box] Box262  label="Cube221"
  AttacherType = Attacher::AttachEngine3D
  Height = 7
  Length = 10
  Placement = pos=(-15,34.6,-2) rot=(0,0,1;0rad)
  Width = 2
FEATURE [Part::Box] Box263  label="Cube222"
  AttacherType = Attacher::AttachEngine3D
  Height = 7
  Length = 10
  Placement = pos=(-15,25.4,-2) rot=(0,0,1;0rad)
  Width = 2
FEATURE [Part::MultiFuse] Fusion096
  Shapes = -> [Box255,Box258,Box252,Box263,Box262]
FEATURE [Part::Box] Box264  label="Cube223"
  AttacherType = Attacher::AttachEngine3D
  Height = 7
  Length = 4
  Placement = pos=(-6,36.6,-2) rot=(0,0,1;0rad)
  Width = 1
FEATURE [Part::MultiFuse] Fusion095  label="Extra Holes for Clips008"
  Shapes = -> [Box256,Box253,Box264,Box257,Box260,Box259]
FEATURE [Part::Fuse] Fusion098  label="Bumps008"
  Base = -> Sphere079
  Tool = -> Sphere081
FEATURE [Part::Fuse] Fusion094
  Base = -> Fusion098
  Tool = -> Fusion096
FEATURE [Part::Sphere] Sphere082
  Angle1 = -90
  Angle2 = 90
  Angle3 = 360
  AttacherType = Attacher::AttachEngine3D
  Placement = pos=(-7.5,34,0.5) rot=(0,0,1;0rad)
  Radius = 1.5
FEATURE [Part::Fuse] Fusion097  label="Holes008"
  Base = -> Sphere080
  Tool = -> Sphere082
FEATURE [Part::Cut] Cut101
  Base = -> Fusion094
  Tool = -> Fusion097
FEATURE [Part::Cut] Cut097
  Base = -> Cut101
  Tool = -> Fusion095
FEATURE [Part::Cut] Cut098
  Base = -> Cut097
  Tool = -> Box261
FEATURE [Part::Cut] Cut099
  Base = -> Cut098
  Tool = -> Box251
FEATURE [Part::Cut] Cut100  label="Edge Clips006"
  Base = -> Cut099
  Placement = pos=(0,40,0) rot=(0,0,-1;1.5708rad)
  Tool = -> Box254
FEATURE [Part::Cut] Cut102
  Base = -> Box075
  Tool = -> Fusion047
FEATURE [Part::Box] Box265  label="Cube224"
  AttacherType = Attacher::AttachEngine3D
  Height = 10
  Length = 10
  Placement = pos=(24,-6,1) rot=(0.205904,-0.974848,-0.085288;0.803573rad)
  Width = 15
FEATURE [Part::Box] Box266  label="Cube225"
  AttacherType = Attacher::AttachEngine3D
  Height = 10
  Length = 10
  Placement = pos=(-6,16,1) rot=(-0.273007,-0.419215,-0.865867;1.78566rad)
  Width = 15
FEATURE [Part::Box] Box267  label="Cube226"
  AttacherType = Attacher::AttachEngine3D
  Height = 10
  Length = 10
  Placement = pos=(16,46,1) rot=(0.381439,0.080566,0.920876;3.07487rad)
  Width = 15
FEATURE [Part::Box] Box268  label="Cube227"
  AttacherType = Attacher::AttachEngine3D
  Height = 10
  Length = 10
  Placement = pos=(46,24,1) rot=(0.442189,-0.287968,0.849437;1.66134rad)
  Width = 15
FEATURE [Part::MultiFuse] Fusion099  label="Glue Dents001"
  Shapes = -> [Box265,Box266,Box267,Box268]
FEATURE [Part::MultiFuse] Fusion100
  Shapes = -> [Cut100,Cut086,Cut091,Cut092]
FEATURE [Part::Fuse] Fusion101
  Base = -> Cut102
  Tool = -> Fusion100
FEATURE [Part::Cut] Cut103  label="Nut Plate"
  Base = -> Fusion101
  Tool = -> Fusion099
FEATURE [Drawing::FeatureViewAnnotation] Annotation001
  Font = Sans
  Rotation = 0
  Scale = 7
  Text = 0.5 rejigged whole thing, stopped clips overhang and moved bump and holes back 0.5
  ViewResult = <g transform="translate(14,30) rotate(0)">\n<text id="Annotation001"\n font-family="Sans"\n font-size="7"\n fill="#000000">\n<tspan x="0" dy="1em">0.5 rejigged whole thing, stopped clips overhang and moved bump and holes back 0.5</tspan>\n</text>\n</g>
  Visible = false
  X = 14
  Y = 30
FEATURE [Drawing::FeaturePage] Page
  EditableTexts = AUTHOR NAME | CREATION DATE | SUPERVISOR NAME | CHECK DATE | SCALE | WEIGHT | NUMBER | SHEET | TITLE | SUBTITLE
  Group = -> [Annotation,Annotation001]
  Template = <path>
FEATURE [Part::Cut] Cut104
  Base = -> Cut103
  Tool = -> Chamfer014
FEATURE [Part::Cut] Cut105
  Base = -> Cut104
  Tool = -> Chamfer013
FEATURE [Part::Cut] Cut106  label="Nut Plate001"
  Base = -> Cut105
  Tool = -> Box145
FEATURE [Part::Sphere] Sphere083
  Angle1 = -90
  Angle2 = 90
  Angle3 = 360
  AttacherType = Attacher::AttachEngine3D
  Placement = pos=(-7.5,34,0.5) rot=(0,0,1;0rad)
  Radius = 1.5
FEATURE [Part::Box] Box269  label="Cube228"
  AttacherType = Attacher::AttachEngine3D
  Height = 7
  Length = 4
  Placement = pos=(-6,27.4,-2) rot=(0,0,1;0rad)
  Width = 7.2
FEATURE [Part::Box] Box270  label="Cube229"
  AttacherType = Attacher::AttachEngine3D
  Height = 7
  Length = 4
  Placement = pos=(-6,24.4,-2) rot=(0,0,1;0rad)
  Width = 1
FEATURE [Part::Sphere] Sphere084  label="Mag Hole 004"
  Angle1 = -90
  Angle2 = 90
  Angle3 = 360
  AttacherType = Attacher::AttachEngine3D
  Placement = pos=(6,34,1.7) rot=(0,0,1;0rad)
  Radius = 2.85
FEATURE [Part::Box] Box271  label="Cube230"
  AttacherType = Attacher::AttachEngine3D
  Height = 7
  Length = 5
  Placement = pos=(-5,0,-2) rot=(0,0,1;0rad)
  Width = 40
FEATURE [Part::Box] Box272  label="Cube231"
  AttacherType = Attacher::AttachEngine3D
  Height = 5
  Length = 40
  Placement = pos=(0,0,-2) rot=(0,0,1;0rad)
  Width = 40
FEATURE [Part::Box] Box273  label="Cube232"
  AttacherType = Attacher::AttachEngine3D
  Height = 7
  Length = 4
  Placement = pos=(-6,36.6,-2) rot=(0,0,1;0rad)
  Width = 1
FEATURE [Part::Sphere] Sphere085
  Angle1 = -90
  Angle2 = 90
  Angle3 = 360
  AttacherType = Attacher::AttachEngine3D
  Placement = pos=(-7.5,11.5,0.5) rot=(0,0,1;0rad)
  Radius = 1.25
FEATURE [Part::Box] Box274  label="Cube233"
  AttacherType = Attacher::AttachEngine3D
  Height = 7
  Length = 4
  Placement = pos=(-6,12,-2) rot=(0,0,1;0rad)
  Width = 1
FEATURE [Part::Box] Box275  label="Re-level Edge Clip Block018"
  AttacherType = Attacher::AttachEngine3D
  Height = 10
  Length = 20
  Placement = pos=(-19,-2,3) rot=(0,0,1;0rad)
  Width = 44
FEATURE [Part::Box] Box276  label="Cube234"
  AttacherType = Attacher::AttachEngine3D
  Height = 7
  Length = 10
  Placement = pos=(-15,25.4,-2) rot=(0,0,1;0rad)
  Width = 2
FEATURE [Part::Box] Box277  label="Chamfer Cube009"
  AttacherType = Attacher::AttachEngine3D
  Height = 10
  Length = 13
  Placement = pos=(-11.69,0,-1.19) rot=(0,-1,0;0.785398rad)
  Width = 40
FEATURE [Part::Box] Box278  label="Cube235"
  AttacherType = Attacher::AttachEngine3D
  Height = 7
  Length = 4
  Placement = pos=(-6,5,-2) rot=(0,0,1;0rad)
  Width = 1
FEATURE [Part::Box] Box279  label="Cube236"
  AttacherType = Attacher::AttachEngine3D
  Height = 7
  Length = 10
  Placement = pos=(-15,6,-2) rot=(0,0,1;0rad)
  Width = 2
FEATURE [Part::Sphere] Sphere086  label="Mag Hole 005"
  Angle1 = -90
  Angle2 = 90
  Angle3 = 360
  AttacherType = Attacher::AttachEngine3D
  Placement = pos=(34,20,1.7) rot=(0,0,1;0rad)
  Radius = 2.85
FEATURE [Part::Sphere] Sphere087
  Angle1 = -90
  Angle2 = 90
  Angle3 = 360
  AttacherType = Attacher::AttachEngine3D
  Placement = pos=(-7.5,28,0.5) rot=(0,0,1;0rad)
  Radius = 1.5
FEATURE [Part::Box] Box280  label="Cube237"
  AttacherType = Attacher::AttachEngine3D
  Height = 7
  Length = 10
  Placement = pos=(-15,34.6,-2) rot=(0,0,1;0rad)
  Width = 2
FEATURE [Part::Sphere] Sphere088
  Angle1 = -90
  Angle2 = 90
  Angle3 = 360
  AttacherType = Attacher::AttachEngine3D
  Placement = pos=(-7.5,6.5,0.5) rot=(0,0,1;0rad)
  Radius = 1.25
FEATURE [Part::Box] Box281  label="Cube238"
  AttacherType = Attacher::AttachEngine3D
  Height = 7
  Length = 10
  Placement = pos=(-15,10,-2) rot=(0,0,1;0rad)
  Width = 2
FEATURE [Part::Box] Box282  label="Cube239"
  AttacherType = Attacher::AttachEngine3D
  Height = 7
  Length = 4
  Placement = pos=(-6,8,-2) rot=(0,0,1;0rad)
  Width = 2
FEATURE [Part::MultiFuse] Fusion103  label="Extra Holes for Clips009"
  Shapes = -> [Box269,Box274,Box273,Box282,Box270,Box278]
FEATURE [Part::Sphere] Sphere089  label="Mag Hole001"
  Angle1 = -90
  Angle2 = 90
  Angle3 = 360
  AttacherType = Attacher::AttachEngine3D
  Placement = pos=(6,6,1.7) rot=(0,0,1;0rad)
  Radius = 2.85
FEATURE [Part::MultiFuse] Fusion102
  Shapes = -> [Sphere089,Sphere086,Sphere084]
FEATURE [Part::Cut] Cut108
  Base = -> Box272
  Tool = -> Fusion102
FEATURE [Part::Box] Box283  label="Cube240"
  AttacherType = Attacher::AttachEngine3D
  Height = 15
  Length = 16.5
  Placement = pos=(11.75,11.75,-3) rot=(0,0,1;0rad)
  Width = 16.5
FEATURE [Part::Box] Box284  label="Cube241"
  AttacherType = Attacher::AttachEngine3D
  Height = 10
  Length = 21
  Placement = pos=(9.5,9.5,2.1) rot=(0,0,1;0rad)
  Width = 21
FEATURE [Part::Box] Box285  label="Cube242"
  AttacherType = Attacher::AttachEngine3D
  Height = 14
  Length = 17
  Placement = pos=(11.5,11.5,0) rot=(0,0,1;0rad)
  Width = 17
FEATURE [Part::Cut] Cut107
  Base = -> Box284
  Tool = -> Box285
FEATURE [Part::Chamfer] Chamfer015
  Base = -> Cut107
  Edges = 8 edges r=0.95: [Edge4,Edge5,Edge14,Edge16,Edge17,Edge18,Edge19,Edge20]
FEATURE [Part::Chamfer] Chamfer016
  Base = -> Box283
  Edges = 4 edges r=4: [Edge1,Edge3,Edge5,Edge7]
FEATURE [Part::Box] Box286  label="Cube243"
  AttacherType = Attacher::AttachEngine3D
  Height = 15
  Length = 16
  Placement = pos=(12,12,-13) rot=(0,0,1;0rad)
  Width = 16
FEATURE [Part::Box] Box287  label="Cube244"
  AttacherType = Attacher::AttachEngine3D
  Height = 10
  Length = 10
  Placement = pos=(24,-6,1) rot=(0.205904,-0.974848,-0.085288;0.803573rad)
  Width = 15
FEATURE [Part::Cut] Cut109
  Base = -> Cut108
  Tool = -> Chamfer015
FEATURE [Part::Cut] Cut110
  Base = -> Cut109
  Tool = -> Chamfer016
FEATURE [Part::Cut] Cut111  label="Centre Block001"
  Base = -> Cut110
  Tool = -> Box286
FEATURE [Part::Cylinder] Cylinder027
  Angle = 360
  AttacherType = Attacher::AttachEngine3D
  Height = 10
  Placement = pos=(6,6,-5) rot=(0,0,1;0rad)
  Radius = 1.7
FEATURE [Part::Cylinder] Cylinder028
  Angle = 360
  AttacherType = Attacher::AttachEngine3D
  Height = 10
  Placement = pos=(34,20,-5) rot=(0,0,1;0rad)
  Radius = 1.7
FEATURE [Part::Cylinder] Cylinder029
  Angle = 360
  AttacherType = Attacher::AttachEngine3D
  Height = 10
  Placement = pos=(6,34,-5) rot=(0,0,1;0rad)
  Radius = 1.7
FEATURE [Part::MultiFuse] Fusion104  label="Screw Holes to remove ball mags001"
  Shapes = -> [Cylinder027,Cylinder028,Cylinder029]
FEATURE [Part::Box] Box288  label="Re-level Edge Clip Block019"
  AttacherType = Attacher::AttachEngine3D
  Height = 10
  Length = 12
  Placement = pos=(-21.5,-2,-7) rot=(0,0,1;0rad)
  Width = 44
FEATURE [Part::Fuse] Fusion105  label="Bumps009"
  Base = -> Sphere088
  Tool = -> Sphere085
FEATURE [Part::Fuse] Fusion106  label="Holes009"
  Base = -> Sphere087
  Tool = -> Sphere083
FEATURE [Part::MultiFuse] Fusion107
  Shapes = -> [Box271,Box279,Box281,Box276,Box280]
FEATURE [Part::Fuse] Fusion108
  Base = -> Fusion105
  Tool = -> Fusion107
FEATURE [Part::Cut] Cut112
  Base = -> Fusion108
  Tool = -> Fusion106
FEATURE [Part::Cut] Cut113
  Base = -> Cut112
  Tool = -> Fusion103
FEATURE [Part::Cut] Cut114
  Base = -> Cut113
  Tool = -> Box275
FEATURE [Part::Cut] Cut115
  Base = -> Cut114
  Tool = -> Box288
FEATURE [Part::Cut] Cut116  label="Edge Clips Master002"
  Base = -> Cut115
  Tool = -> Box277
FEATURE [Part::Box] Box289  label="Cube245"
  AttacherType = Attacher::AttachEngine3D
  Height = 7
  Length = 5
  Placement = pos=(-5,0,-2) rot=(0,0,1;0rad)
  Width = 40
FEATURE [Part::Box] Box290  label="Cube246"
  AttacherType = Attacher::AttachEngine3D
  Height = 7
  Length = 10
  Placement = pos=(-15,6,-2) rot=(0,0,1;0rad)
  Width = 2
FEATURE [Part::Box] Box291  label="Cube247"
  AttacherType = Attacher::AttachEngine3D
  Height = 7
  Length = 10
  Placement = pos=(-15,10,-2) rot=(0,0,1;0rad)
  Width = 2
FEATURE [Part::Box] Box292  label="Cube248"
  AttacherType = Attacher::AttachEngine3D
  Height = 7
  Length = 10
  Placement = pos=(-15,25.4,-2) rot=(0,0,1;0rad)
  Width = 2
FEATURE [Part::Box] Box293  label="Cube249"
  AttacherType = Attacher::AttachEngine3D
  Height = 7
  Length = 10
  Placement = pos=(-15,34.6,-2) rot=(0,0,1;0rad)
  Width = 2
FEATURE [Part::Sphere] Sphere090
  Angle1 = -90
  Angle2 = 90
  Angle3 = 360
  AttacherType = Attacher::AttachEngine3D
  Placement = pos=(-7.5,6.5,0.5) rot=(0,0,1;0rad)
  Radius = 1.25
FEATURE [Part::Box] Box294  label="Chamfer Cube010"
  AttacherType = Attacher::AttachEngine3D
  Height = 10
  Length = 13
  Placement = pos=(-11.69,0,-1.19) rot=(0,-1,0;0.785398rad)
  Width = 40
FEATURE [Part::Sphere] Sphere091
  Angle1 = -90
  Angle2 = 90
  Angle3 = 360
  AttacherType = Attacher::AttachEngine3D
  Placement = pos=(-7.5,11.5,0.5) rot=(0,0,1;0rad)
  Radius = 1.25
FEATURE [Part::Sphere] Sphere092
  Angle1 = -90
  Angle2 = 90
  Angle3 = 360
  AttacherType = Attacher::AttachEngine3D
  Placement = pos=(-7.5,28,0.5) rot=(0,0,1;0rad)
  Radius = 1.5
FEATURE [Part::Sphere] Sphere093
  Angle1 = -90
  Angle2 = 90
  Angle3 = 360
  AttacherType = Attacher::AttachEngine3D
  Placement = pos=(-7.5,34,0.5) rot=(0,0,1;0rad)
  Radius = 1.5
FEATURE [Part::Box] Box295  label="Cube250"
  AttacherType = Attacher::AttachEngine3D
  Height = 7
  Length = 4
  Placement = pos=(-6,5,-2) rot=(0,0,1;0rad)
  Width = 1
FEATURE [Part::Box] Box296  label="Cube251"
  AttacherType = Attacher::AttachEngine3D
  Height = 7
  Length = 4
  Placement = pos=(-6,8,-2) rot=(0,0,1;0rad)
  Width = 2
FEATURE [Part::Box] Box297  label="Cube252"
  AttacherType = Attacher::AttachEngine3D
  Height = 7
  Length = 4
  Placement = pos=(-6,12,-2) rot=(0,0,1;0rad)
  Width = 1
FEATURE [Part::Box] Box298  label="Cube253"
  AttacherType = Attacher::AttachEngine3D
  Height = 7
  Length = 4
  Placement = pos=(-6,24.4,-2) rot=(0,0,1;0rad)
  Width = 1
FEATURE [Part::Box] Box299  label="Cube254"
  AttacherType = Attacher::AttachEngine3D
  Height = 7
  Length = 4
  Placement = pos=(-6,36.6,-2) rot=(0,0,1;0rad)
  Width = 1
FEATURE [Part::Box] Box300  label="Cube255"
  AttacherType = Attacher::AttachEngine3D
  Height = 7
  Length = 4
  Placement = pos=(-6,27.4,-2) rot=(0,0,1;0rad)
  Width = 7.2
FEATURE [Part::MultiFuse] Fusion109  label="Extra Holes for Clips010"
  Shapes = -> [Box300,Box297,Box299,Box296,Box298,Box295]
FEATURE [Part::Box] Box301  label="Re-level Edge Clip Block020"
  AttacherType = Attacher::AttachEngine3D
  Height = 10
  Length = 20
  Placement = pos=(-19,-2,3) rot=(0,0,1;0rad)
  Width = 44
FEATURE [Part::Box] Box302  label="Re-level Edge Clip Block021"
  AttacherType = Attacher::AttachEngine3D
  Height = 10
  Length = 12
  Placement = pos=(-21.5,-2,-7) rot=(0,0,1;0rad)
  Width = 44
FEATURE [Part::Fuse] Fusion110  label="Bumps010"
  Base = -> Sphere090
  Tool = -> Sphere091
FEATURE [Part::Fuse] Fusion111  label="Holes010"
  Base = -> Sphere092
  Tool = -> Sphere093
FEATURE [Part::MultiFuse] Fusion112
  Shapes = -> [Box289,Box290,Box291,Box292,Box293]
FEATURE [Part::Fuse] Fusion113
  Base = -> Fusion110
  Tool = -> Fusion112
FEATURE [Part::Cut] Cut117
  Base = -> Fusion113
  Tool = -> Fusion111
FEATURE [Part::Cut] Cut118
  Base = -> Cut117
  Tool = -> Fusion109
FEATURE [Part::Cut] Cut119
  Base = -> Cut118
  Tool = -> Box301
FEATURE [Part::Cut] Cut120
  Base = -> Cut119
  Tool = -> Box302
FEATURE [Part::Cut] Cut121  label="Edge Clips007"
  Base = -> Cut120
  Placement = pos=(40,0,0) rot=(0,0,1;1.5708rad)
  Tool = -> Box294
FEATURE [Part::Box] Box303  label="Cube256"
  AttacherType = Attacher::AttachEngine3D
  Height = 7
  Length = 5
  Placement = pos=(-5,0,-2) rot=(0,0,1;0rad)
  Width = 40
FEATURE [Part::Box] Box304  label="Cube257"
  AttacherType = Attacher::AttachEngine3D
  Height = 7
  Length = 10
  Placement = pos=(-15,10,-2) rot=(0,0,1;0rad)
  Width = 2
FEATURE [Part::Box] Box305  label="Re-level Edge Clip Block022"
  AttacherType = Attacher::AttachEngine3D
  Height = 10
  Length = 20
  Placement = pos=(-19,-2,3) rot=(0,0,1;0rad)
  Width = 44
FEATURE [Part::Box] Box306  label="Cube258"
  AttacherType = Attacher::AttachEngine3D
  Height = 7
  Length = 4
  Placement = pos=(-6,27.4,-2) rot=(0,0,1;0rad)
  Width = 7.2
FEATURE [Part::Box] Box307  label="Cube259"
  AttacherType = Attacher::AttachEngine3D
  Height = 7
  Length = 4
  Placement = pos=(-6,12,-2) rot=(0,0,1;0rad)
  Width = 1
FEATURE [Part::Sphere] Sphere094
  Angle1 = -90
  Angle2 = 90
  Angle3 = 360
  AttacherType = Attacher::AttachEngine3D
  Placement = pos=(-7.5,6.5,0.5) rot=(0,0,1;0rad)
  Radius = 1.25
FEATURE [Part::Box] Box308  label="Cube260"
  AttacherType = Attacher::AttachEngine3D
  Height = 7
  Length = 10
  Placement = pos=(-15,25.4,-2) rot=(0,0,1;0rad)
  Width = 2
FEATURE [Part::Box] Box309  label="Cube261"
  AttacherType = Attacher::AttachEngine3D
  Height = 7
  Length = 4
  Placement = pos=(-6,36.6,-2) rot=(0,0,1;0rad)
  Width = 1
FEATURE [Part::Sphere] Sphere095
  Angle1 = -90
  Angle2 = 90
  Angle3 = 360
  AttacherType = Attacher::AttachEngine3D
  Placement = pos=(-7.5,34,0.5) rot=(0,0,1;0rad)
  Radius = 1.5
FEATURE [Part::Box] Box310  label="Cube262"
  AttacherType = Attacher::AttachEngine3D
  Height = 7
  Length = 4
  Placement = pos=(-6,24.4,-2) rot=(0,0,1;0rad)
  Width = 1
FEATURE [Part::Box] Box311  label="Cube263"
  AttacherType = Attacher::AttachEngine3D
  Height = 7
  Length = 4
  Placement = pos=(-6,8,-2) rot=(0,0,1;0rad)
  Width = 2
FEATURE [Part::Box] Box312  label="Re-level Edge Clip Block023"
  AttacherType = Attacher::AttachEngine3D
  Height = 10
  Length = 12
  Placement = pos=(-21.5,-2,-7) rot=(0,0,1;0rad)
  Width = 44
FEATURE [Part::Sphere] Sphere096
  Angle1 = -90
  Angle2 = 90
  Angle3 = 360
  AttacherType = Attacher::AttachEngine3D
  Placement = pos=(-7.5,11.5,0.5) rot=(0,0,1;0rad)
  Radius = 1.25
FEATURE [Part::Sphere] Sphere097
  Angle1 = -90
  Angle2 = 90
  Angle3 = 360
  AttacherType = Attacher::AttachEngine3D
  Placement = pos=(-7.5,28,0.5) rot=(0,0,1;0rad)
  Radius = 1.5
FEATURE [Part::Fuse] Fusion114  label="Holes011"
  Base = -> Sphere097
  Tool = -> Sphere095
FEATURE [Part::Box] Box313  label="Cube264"
  AttacherType = Attacher::AttachEngine3D
  Height = 7
  Length = 10
  Placement = pos=(-15,34.6,-2) rot=(0,0,1;0rad)
  Width = 2
FEATURE [Part::Box] Box314  label="Cube265"
  AttacherType = Attacher::AttachEngine3D
  Height = 7
  Length = 4
  Placement = pos=(-6,5,-2) rot=(0,0,1;0rad)
  Width = 1
FEATURE [Part::MultiFuse] Fusion115  label="Extra Holes for Clips011"
  Shapes = -> [Box306,Box307,Box309,Box311,Box310,Box314]
FEATURE [Part::Box] Box315  label="Cube266"
  AttacherType = Attacher::AttachEngine3D
  Height = 7
  Length = 10
  Placement = pos=(-15,6,-2) rot=(0,0,1;0rad)
  Width = 2
FEATURE [Part::MultiFuse] Fusion117
  Shapes = -> [Box303,Box315,Box304,Box308,Box313]
FEATURE [Part::Fuse] Fusion118  label="Bumps011"
  Base = -> Sphere094
  Tool = -> Sphere096
FEATURE [Part::Fuse] Fusion116
  Base = -> Fusion118
  Tool = -> Fusion117
FEATURE [Part::Cut] Cut125
  Base = -> Fusion116
  Tool = -> Fusion114
FEATURE [Part::Cut] Cut122
  Base = -> Cut125
  Tool = -> Fusion115
FEATURE [Part::Cut] Cut123
  Base = -> Cut122
  Tool = -> Box305
FEATURE [Part::Cut] Cut124
  Base = -> Cut123
  Tool = -> Box312
FEATURE [Part::Box] Box316  label="Chamfer Cube011"
  AttacherType = Attacher::AttachEngine3D
  Height = 10
  Length = 13
  Placement = pos=(-11.69,0,-1.19) rot=(0,-1,0;0.785398rad)
  Width = 40
FEATURE [Part::Cut] Cut126  label="Edge Clips008"
  Base = -> Cut124
  Placement = pos=(40,40,0) rot=(0,0,1;3.14159rad)
  Tool = -> Box316
FEATURE [Part::Box] Box317  label="Cube267"
  AttacherType = Attacher::AttachEngine3D
  Height = 7
  Length = 10
  Placement = pos=(-15,6,-2) rot=(0,0,1;0rad)
  Width = 2
FEATURE [Part::Box] Box318  label="Chamfer Cube012"
  AttacherType = Attacher::AttachEngine3D
  Height = 10
  Length = 13
  Placement = pos=(-11.69,0,-1.19) rot=(0,-1,0;0.785398rad)
  Width = 40
FEATURE [Part::Box] Box319  label="Re-level Edge Clip Block024"
  AttacherType = Attacher::AttachEngine3D
  Height = 10
  Length = 20
  Placement = pos=(-19,-2,3) rot=(0,0,1;0rad)
  Width = 44
FEATURE [Part::Box] Box320  label="Cube268"
  AttacherType = Attacher::AttachEngine3D
  Height = 7
  Length = 10
  Placement = pos=(-15,10,-2) rot=(0,0,1;0rad)
  Width = 2
FEATURE [Part::Box] Box321  label="Cube269"
  AttacherType = Attacher::AttachEngine3D
  Height = 7
  Length = 5
  Placement = pos=(-5,0,-2) rot=(0,0,1;0rad)
  Width = 40
FEATURE [Part::Box] Box322  label="Cube270"
  AttacherType = Attacher::AttachEngine3D
  Height = 7
  Length = 4
  Placement = pos=(-6,5,-2) rot=(0,0,1;0rad)
  Width = 1
FEATURE [Part::Box] Box323  label="Cube271"
  AttacherType = Attacher::AttachEngine3D
  Height = 7
  Length = 4
  Placement = pos=(-6,12,-2) rot=(0,0,1;0rad)
  Width = 1
FEATURE [Part::Box] Box324  label="Cube272"
  AttacherType = Attacher::AttachEngine3D
  Height = 7
  Length = 4
  Placement = pos=(-6,27.4,-2) rot=(0,0,1;0rad)
  Width = 7.2
FEATURE [Part::Box] Box325  label="Cube273"
  AttacherType = Attacher::AttachEngine3D
  Height = 7
  Length = 4
  Placement = pos=(-6,24.4,-2) rot=(0,0,1;0rad)
  Width = 1
FEATURE [Part::Sphere] Sphere098
  Angle1 = -90
  Angle2 = 90
  Angle3 = 360
  AttacherType = Attacher::AttachEngine3D
  Placement = pos=(-7.5,28,0.5) rot=(0,0,1;0rad)
  Radius = 1.5
FEATURE [Part::Sphere] Sphere099
  Angle1 = -90
  Angle2 = 90
  Angle3 = 360
  AttacherType = Attacher::AttachEngine3D
  Placement = pos=(-7.5,11.5,0.5) rot=(0,0,1;0rad)
  Radius = 1.25
FEATURE [Part::Box] Box326  label="Cube274"
  AttacherType = Attacher::AttachEngine3D
  Height = 7
  Length = 4
  Placement = pos=(-6,8,-2) rot=(0,0,1;0rad)
  Width = 2
FEATURE [Part::Box] Box327  label="Cube275"
  AttacherType = Attacher::AttachEngine3D
  Height = 7
  Length = 10
  Placement = pos=(-15,25.4,-2) rot=(0,0,1;0rad)
  Width = 2
FEATURE [Part::Sphere] Sphere100
  Angle1 = -90
  Angle2 = 90
  Angle3 = 360
  AttacherType = Attacher::AttachEngine3D
  Placement = pos=(-7.5,6.5,0.5) rot=(0,0,1;0rad)
  Radius = 1.25
FEATURE [Part::Fuse] Fusion121  label="Bumps012"
  Base = -> Sphere100
  Tool = -> Sphere099
FEATURE [Part::Sphere] Sphere101
  Angle1 = -90
  Angle2 = 90
  Angle3 = 360
  AttacherType = Attacher::AttachEngine3D
  Placement = pos=(-7.5,34,0.5) rot=(0,0,1;0rad)
  Radius = 1.5
FEATURE [Part::Fuse] Fusion119  label="Holes012"
  Base = -> Sphere098
  Tool = -> Sphere101
FEATURE [Part::Box] Box328  label="Re-level Edge Clip Block025"
  AttacherType = Attacher::AttachEngine3D
  Height = 10
  Length = 12
  Placement = pos=(-21.5,-2,-7) rot=(0,0,1;0rad)
  Width = 44
FEATURE [Part::Box] Box329  label="Cube276"
  AttacherType = Attacher::AttachEngine3D
  Height = 7
  Length = 4
  Placement = pos=(-6,36.6,-2) rot=(0,0,1;0rad)
  Width = 1
FEATURE [Part::MultiFuse] Fusion122  label="Extra Holes for Clips012"
  Shapes = -> [Box324,Box323,Box329,Box326,Box325,Box322]
FEATURE [Part::Box] Box330  label="Cube277"
  AttacherType = Attacher::AttachEngine3D
  Height = 7
  Length = 10
  Placement = pos=(-15,34.6,-2) rot=(0,0,1;0rad)
  Width = 2
FEATURE [Part::MultiFuse] Fusion120
  Shapes = -> [Box321,Box317,Box320,Box327,Box330]
FEATURE [Part::Fuse] Fusion123
  Base = -> Fusion121
  Tool = -> Fusion120
FEATURE [Part::Cut] Cut127
  Base = -> Fusion123
  Tool = -> Fusion119
FEATURE [Part::Cut] Cut128
  Base = -> Cut127
  Tool = -> Fusion122
FEATURE [Part::Cut] Cut130
  Base = -> Cut128
  Tool = -> Box319
FEATURE [Part::Cut] Cut129
  Base = -> Cut130
  Tool = -> Box328
FEATURE [Part::Cut] Cut131  label="Edge Clips009"
  Base = -> Cut129
  Placement = pos=(0,40,0) rot=(0,0,-1;1.5708rad)
  Tool = -> Box318
FEATURE [Part::MultiFuse] Fusion124  label="Edge Clips Fusion001"
  Shapes = -> [Cut116,Cut121,Cut126,Cut131]
FEATURE [Part::Cut] Cut132
  Base = -> Cut111
  Tool = -> Fusion104
FEATURE [Part::Fuse] Fusion125
  Base = -> Fusion124
  Tool = -> Cut132
FEATURE [Part::Box] Box331  label="Cube278"
  AttacherType = Attacher::AttachEngine3D
  Height = 10
  Length = 10
  Placement = pos=(46,24,1) rot=(0.442189,-0.287968,0.849437;1.66134rad)
  Width = 15
FEATURE [Part::Box] Box332  label="Cube279"
  AttacherType = Attacher::AttachEngine3D
  Height = 10
  Length = 10
  Placement = pos=(16,46,1) rot=(0.381439,0.080566,0.920876;3.07487rad)
  Width = 15
FEATURE [Part::Box] Box333  label="Cube280"
  AttacherType = Attacher::AttachEngine3D
  Height = 10
  Length = 10
  Placement = pos=(-6,16,1) rot=(-0.273007,-0.419215,-0.865867;1.78566rad)
  Width = 15
FEATURE [Part::MultiFuse] Fusion126  label="Glue Dents002"
  Shapes = -> [Box287,Box333,Box332,Box331]
FEATURE [Part::Cut] Cut133  label="Ball Plate001"
  Base = -> Fusion125
  Placement = pos=(59.97,0,0) rot=(0,0,1;0rad)
  Tool = -> Fusion126
FEATURE [Part::Box] Box334  label="Square Nut Hole 024"
  AttacherType = Attacher::AttachEngine3D
  Height = 2
  Length = 5.8
  Placement = pos=(31.1,17.1,4.6) rot=(0,0,1;0rad)
  Width = 5.8
FEATURE [Part::Box] Box335  label="Square Nut Hole 025"
  AttacherType = Attacher::AttachEngine3D
  Height = 2
  Length = 5.8
  Placement = pos=(17.1,3.1,4.6) rot=(0,0,1;0rad)
  Width = 5.8
FEATURE [Part::Box] Box336  label="Square Nut Hole 026"
  AttacherType = Attacher::AttachEngine3D
  Height = 2
  Length = 5.8
  Placement = pos=(31.1,3.1,4.6) rot=(0,0,1;0rad)
  Width = 5.8
FEATURE [Part::Box] Box337  label="Square Nut Hole 027"
  AttacherType = Attacher::AttachEngine3D
  Height = 2
  Length = 5.8
  Placement = pos=(3.1,3.1,4.6) rot=(0,0,1;0rad)
  Width = 5.8
FEATURE [Part::Box] Box338  label="Square Nut Hole 028"
  AttacherType = Attacher::AttachEngine3D
  Height = 2
  Length = 5.8
  Placement = pos=(3.1,31.1,4.6) rot=(0,0,1;0rad)
  Width = 5.8
FEATURE [Part::Box] Box339  label="Square Nut Hole 029"
  AttacherType = Attacher::AttachEngine3D
  Height = 2
  Length = 5.8
  Placement = pos=(17.1,31.1,4.6) rot=(0,0,1;0rad)
  Width = 5.8
FEATURE [Part::Box] Box340  label="Square Nut Hole 030"
  AttacherType = Attacher::AttachEngine3D
  Height = 2
  Length = 5.8
  Placement = pos=(31.1,31.1,4.6) rot=(0,0,1;0rad)
  Width = 5.8
FEATURE [Part::Box] Box341  label="Square Nut Hole 031"
  AttacherType = Attacher::AttachEngine3D
  Height = 2
  Length = 5.8
  Placement = pos=(3.1,17.1,4.6) rot=(0,0,1;0rad)
  Width = 5.8
FEATURE [Part::Cylinder] Cylinder030
  Angle = 360
  AttacherType = Attacher::AttachEngine3D
  Height = 10
  Placement = pos=(6,6,0) rot=(0,0,1;0rad)
  Radius = 1.7
FEATURE [Part::Cylinder] Cylinder031
  Angle = 360
  AttacherType = Attacher::AttachEngine3D
  Height = 10
  Placement = pos=(34,34,0) rot=(0,0,1;0rad)
  Radius = 1.7
FEATURE [Part::Cylinder] Cylinder032
  Angle = 360
  AttacherType = Attacher::AttachEngine3D
  Height = 10
  Placement = pos=(20,34,0) rot=(0,0,1;0rad)
  Radius = 1.7
FEATURE [Part::Cylinder] Cylinder033
  Angle = 360
  AttacherType = Attacher::AttachEngine3D
  Height = 10
  Placement = pos=(6,34,0) rot=(0,0,1;0rad)
  Radius = 1.7
FEATURE [Part::Cylinder] Cylinder034
  Angle = 360
  AttacherType = Attacher::AttachEngine3D
  Height = 10
  Placement = pos=(6,20,0) rot=(0,0,1;0rad)
  Radius = 1.7
FEATURE [Part::Cylinder] Cylinder035
  Angle = 360
  AttacherType = Attacher::AttachEngine3D
  Height = 10
  Placement = pos=(34,20,0) rot=(0,0,1;0rad)
  Radius = 1.7
FEATURE [Part::Cylinder] Cylinder036
  Angle = 360
  AttacherType = Attacher::AttachEngine3D
  Height = 10
  Placement = pos=(34,6,0) rot=(0,0,1;0rad)
  Radius = 1.7
FEATURE [Part::Cylinder] Cylinder037
  Angle = 360
  AttacherType = Attacher::AttachEngine3D
  Height = 10
  Placement = pos=(20,6,0) rot=(0,0,1;0rad)
  Radius = 1.7
FEATURE [Part::Box] Box342  label="Cube281"
  AttacherType = Attacher::AttachEngine3D
  Height = 5
  Length = 40
  Placement = pos=(0,0,-2) rot=(0,0,1;0rad)
  Width = 40
FEATURE [Part::Sphere] Sphere102
  Angle1 = -90
  Angle2 = 90
  Angle3 = 360
  AttacherType = Attacher::AttachEngine3D
  Placement = pos=(34,20,2.4) rot=(0,0,1;0rad)
  Radius = 3.35
FEATURE [Part::Sphere] Sphere103  label="Nut Clearence003"
  Angle1 = -90
  Angle2 = 90
  Angle3 = 360
  AttacherType = Attacher::AttachEngine3D
  Placement = pos=(6,6,2.4) rot=(0,0,1;0rad)
  Radius = 3.35
FEATURE [Part::Sphere] Sphere104
  Angle1 = -90
  Angle2 = 90
  Angle3 = 360
  AttacherType = Attacher::AttachEngine3D
  Placement = pos=(34,34,2.4) rot=(0,0,1;0rad)
  Radius = 3.35
FEATURE [Part::Sphere] Sphere105
  Angle1 = -90
  Angle2 = 90
  Angle3 = 360
  AttacherType = Attacher::AttachEngine3D
  Placement = pos=(34,6,2.4) rot=(0,0,1;0rad)
  Radius = 3.35
FEATURE [Part::Sphere] Sphere106
  Angle1 = -90
  Angle2 = 90
  Angle3 = 360
  AttacherType = Attacher::AttachEngine3D
  Placement = pos=(20,6,2.4) rot=(0,0,1;0rad)
  Radius = 3.35
FEATURE [Part::Sphere] Sphere107
  Angle1 = -90
  Angle2 = 90
  Angle3 = 360
  AttacherType = Attacher::AttachEngine3D
  Placement = pos=(6,34,2.4) rot=(0,0,1;0rad)
  Radius = 3.35
FEATURE [Part::Sphere] Sphere108
  Angle1 = -90
  Angle2 = 90
  Angle3 = 360
  AttacherType = Attacher::AttachEngine3D
  Placement = pos=(6,20,2.4) rot=(0,0,1;0rad)
  Radius = 3.35
FEATURE [Part::Sphere] Sphere109
  Angle1 = -90
  Angle2 = 90
  Angle3 = 360
  AttacherType = Attacher::AttachEngine3D
  Placement = pos=(20,34,2.4) rot=(0,0,1;0rad)
  Radius = 3.35
FEATURE [Part::MultiFuse] Fusion127  label="Square Nut Hole001"
  Shapes = -> [Box334,Box340,Box338,Box336,Box335,Box337,Box339,Box341]
FEATURE [Part::MultiFuse] Fusion128  label="Square Nut Screw Holes001"
  Shapes = -> [Cylinder030,Cylinder036,Cylinder034,Cylinder033,Cylinder032,Cylinder031,Cylinder035,Cylinder037]
FEATURE [Part::MultiFuse] Fusion129  label="Nut Chamfers001"
  Shapes = -> [Sphere102,Sphere103,Sphere104,Sphere106,Sphere107,Sphere108,Sphere109,Sphere105]
FEATURE [Part::MultiFuse] Fusion130
  Placement = pos=(0,40,6.7) rot=(1,0,0;3.14159rad)
  Shapes = -> [Fusion129,Fusion127,Fusion128]
FEATURE [Part::Box] Box343  label="Cube282"
  AttacherType = Attacher::AttachEngine3D
  Height = 15
  Length = 16
  Placement = pos=(12,12,-13) rot=(0,0,1;0rad)
  Width = 16
FEATURE [Part::Box] Box344  label="Cube283"
  AttacherType = Attacher::AttachEngine3D
  Height = 15
  Length = 16.5
  Placement = pos=(11.75,11.75,-3) rot=(0,0,1;0rad)
  Width = 16.5
FEATURE [Part::Chamfer] Chamfer017
  Base = -> Box344
  Edges = 4 edges r=4: [Edge1,Edge3,Edge5,Edge7]
FEATURE [Part::Box] Box345  label="Cube284"
  AttacherType = Attacher::AttachEngine3D
  Height = 10
  Length = 21
  Placement = pos=(9.5,9.5,2.1) rot=(0,0,1;0rad)
  Width = 21
FEATURE [Part::Box] Box346  label="Cube285"
  AttacherType = Attacher::AttachEngine3D
  Height = 14
  Length = 17
  Placement = pos=(11.5,11.5,0) rot=(0,0,1;0rad)
  Width = 17
FEATURE [Part::Cut] Cut134
  Base = -> Box345
  Tool = -> Box346
FEATURE [Part::Chamfer] Chamfer018
  Base = -> Cut134
  Edges = 8 edges r=0.95: [Edge4,Edge5,Edge14,Edge16,Edge17,Edge18,Edge19,Edge20]
FEATURE [Part::Box] Box347  label="Cube286"
  AttacherType = Attacher::AttachEngine3D
  Height = 7
  Length = 5
  Placement = pos=(-5,0,-2) rot=(0,0,1;0rad)
  Width = 40
FEATURE [Part::Box] Box348  label="Cube287"
  AttacherType = Attacher::AttachEngine3D
  Height = 7
  Length = 10
  Placement = pos=(-15,6,-2) rot=(0,0,1;0rad)
  Width = 2
FEATURE [Part::Box] Box349  label="Cube288"
  AttacherType = Attacher::AttachEngine3D
  Height = 7
  Length = 10
  Placement = pos=(-15,10,-2) rot=(0,0,1;0rad)
  Width = 2
FEATURE [Part::Box] Box350  label="Cube289"
  AttacherType = Attacher::AttachEngine3D
  Height = 7
  Length = 10
  Placement = pos=(-15,25.4,-2) rot=(0,0,1;0rad)
  Width = 2
FEATURE [Part::Box] Box351  label="Cube290"
  AttacherType = Attacher::AttachEngine3D
  Height = 7
  Length = 10
  Placement = pos=(-15,34.6,-2) rot=(0,0,1;0rad)
  Width = 2
FEATURE [Part::Sphere] Sphere110
  Angle1 = -90
  Angle2 = 90
  Angle3 = 360
  AttacherType = Attacher::AttachEngine3D
  Placement = pos=(-7.5,6.5,0.5) rot=(0,0,1;0rad)
  Radius = 1.25
FEATURE [Part::Box] Box352  label="Chamfer Cube013"
  AttacherType = Attacher::AttachEngine3D
  Height = 10
  Length = 13
  Placement = pos=(-11.69,0,-1.19) rot=(0,-1,0;0.785398rad)
  Width = 40
FEATURE [Part::Sphere] Sphere111
  Angle1 = -90
  Angle2 = 90
  Angle3 = 360
  AttacherType = Attacher::AttachEngine3D
  Placement = pos=(-7.5,11.5,0.5) rot=(0,0,1;0rad)
  Radius = 1.25
FEATURE [Part::Sphere] Sphere112
  Angle1 = -90
  Angle2 = 90
  Angle3 = 360
  AttacherType = Attacher::AttachEngine3D
  Placement = pos=(-7.5,28,0.5) rot=(0,0,1;0rad)
  Radius = 1.5
FEATURE [Part::Sphere] Sphere113
  Angle1 = -90
  Angle2 = 90
  Angle3 = 360
  AttacherType = Attacher::AttachEngine3D
  Placement = pos=(-7.5,34,0.5) rot=(0,0,1;0rad)
  Radius = 1.5
FEATURE [Part::Box] Box353  label="Cube291"
  AttacherType = Attacher::AttachEngine3D
  Height = 7
  Length = 4
  Placement = pos=(-6,5,-2) rot=(0,0,1;0rad)
  Width = 1
FEATURE [Part::Box] Box354  label="Cube292"
  AttacherType = Attacher::AttachEngine3D
  Height = 7
  Length = 4
  Placement = pos=(-6,8,-2) rot=(0,0,1;0rad)
  Width = 2
FEATURE [Part::Box] Box355  label="Cube293"
  AttacherType = Attacher::AttachEngine3D
  Height = 7
  Length = 4
  Placement = pos=(-6,12,-2) rot=(0,0,1;0rad)
  Width = 1
FEATURE [Part::Box] Box356  label="Cube294"
  AttacherType = Attacher::AttachEngine3D
  Height = 7
  Length = 4
  Placement = pos=(-6,24.4,-2) rot=(0,0,1;0rad)
  Width = 1
FEATURE [Part::Box] Box357  label="Cube295"
  AttacherType = Attacher::AttachEngine3D
  Height = 7
  Length = 4
  Placement = pos=(-6,36.6,-2) rot=(0,0,1;0rad)
  Width = 1
FEATURE [Part::Box] Box358  label="Cube296"
  AttacherType = Attacher::AttachEngine3D
  Height = 7
  Length = 4
  Placement = pos=(-6,27.4,-2) rot=(0,0,1;0rad)
  Width = 7.2
FEATURE [Part::MultiFuse] Fusion131  label="Extra Holes for Clips013"
  Shapes = -> [Box358,Box355,Box357,Box354,Box356,Box353]
FEATURE [Part::Box] Box359  label="Re-level Edge Clip Block026"
  AttacherType = Attacher::AttachEngine3D
  Height = 10
  Length = 20
  Placement = pos=(-19,-2,3) rot=(0,0,1;0rad)
  Width = 44
FEATURE [Part::Box] Box360  label="Re-level Edge Clip Block027"
  AttacherType = Attacher::AttachEngine3D
  Height = 10
  Length = 12
  Placement = pos=(-21.5,-2,-7) rot=(0,0,1;0rad)
  Width = 44
FEATURE [Part::Fuse] Fusion132  label="Bumps013"
  Base = -> Sphere110
  Tool = -> Sphere111
FEATURE [Part::Fuse] Fusion133  label="Holes013"
  Base = -> Sphere112
  Tool = -> Sphere113
FEATURE [Part::MultiFuse] Fusion134
  Shapes = -> [Box347,Box348,Box349,Box350,Box351]
FEATURE [Part::Fuse] Fusion135
  Base = -> Fusion132
  Tool = -> Fusion134
FEATURE [Part::Cut] Cut135
  Base = -> Fusion135
  Tool = -> Fusion133
FEATURE [Part::Cut] Cut136
  Base = -> Cut135
  Tool = -> Fusion131
FEATURE [Part::Cut] Cut137
  Base = -> Cut136
  Tool = -> Box359
FEATURE [Part::Cut] Cut138
  Base = -> Cut137
  Tool = -> Box360
FEATURE [Part::Cut] Cut139  label="Edge Clips Master003"
  Base = -> Cut138
  Tool = -> Box352
FEATURE [Part::Box] Box361  label="Cube297"
  AttacherType = Attacher::AttachEngine3D
  Height = 7
  Length = 5
  Placement = pos=(-5,0,-2) rot=(0,0,1;0rad)
  Width = 40
FEATURE [Part::Box] Box362  label="Cube298"
  AttacherType = Attacher::AttachEngine3D
  Height = 7
  Length = 4
  Placement = pos=(-6,8,-2) rot=(0,0,1;0rad)
  Width = 2
FEATURE [Part::Box] Box363  label="Chamfer Cube014"
  AttacherType = Attacher::AttachEngine3D
  Height = 10
  Length = 13
  Placement = pos=(-11.69,0,-1.19) rot=(0,-1,0;0.785398rad)
  Width = 40
FEATURE [Part::Box] Box364  label="Cube299"
  AttacherType = Attacher::AttachEngine3D
  Height = 7
  Length = 10
  Placement = pos=(-15,6,-2) rot=(0,0,1;0rad)
  Width = 2
FEATURE [Part::Sphere] Sphere114
  Angle1 = -90
  Angle2 = 90
  Angle3 = 360
  AttacherType = Attacher::AttachEngine3D
  Placement = pos=(-7.5,11.5,0.5) rot=(0,0,1;0rad)
  Radius = 1.25
FEATURE [Part::Box] Box365  label="Cube300"
  AttacherType = Attacher::AttachEngine3D
  Height = 7
  Length = 4
  Placement = pos=(-6,27.4,-2) rot=(0,0,1;0rad)
  Width = 7.2
FEATURE [Part::Box] Box366  label="Cube301"
  AttacherType = Attacher::AttachEngine3D
  Height = 7
  Length = 4
  Placement = pos=(-6,12,-2) rot=(0,0,1;0rad)
  Width = 1
FEATURE [Part::Box] Box367  label="Cube302"
  AttacherType = Attacher::AttachEngine3D
  Height = 7
  Length = 4
  Placement = pos=(-6,24.4,-2) rot=(0,0,1;0rad)
  Width = 1
FEATURE [Part::Sphere] Sphere115
  Angle1 = -90
  Angle2 = 90
  Angle3 = 360
  AttacherType = Attacher::AttachEngine3D
  Placement = pos=(-7.5,6.5,0.5) rot=(0,0,1;0rad)
  Radius = 1.25
FEATURE [Part::Box] Box368  label="Cube303"
  AttacherType = Attacher::AttachEngine3D
  Height = 7
  Length = 4
  Placement = pos=(-6,36.6,-2) rot=(0,0,1;0rad)
  Width = 1
FEATURE [Part::Box] Box369  label="Cube304"
  AttacherType = Attacher::AttachEngine3D
  Height = 7
  Length = 10
  Placement = pos=(-15,10,-2) rot=(0,0,1;0rad)
  Width = 2
FEATURE [Part::Sphere] Sphere116
  Angle1 = -90
  Angle2 = 90
  Angle3 = 360
  AttacherType = Attacher::AttachEngine3D
  Placement = pos=(-7.5,34,0.5) rot=(0,0,1;0rad)
  Radius = 1.5
FEATURE [Part::Box] Box370  label="Cube305"
  AttacherType = Attacher::AttachEngine3D
  Height = 7
  Length = 4
  Placement = pos=(-6,5,-2) rot=(0,0,1;0rad)
  Width = 1
FEATURE [Part::MultiFuse] Fusion137  label="Extra Holes for Clips014"
  Shapes = -> [Box365,Box366,Box368,Box362,Box367,Box370]
FEATURE [Part::Box] Box371  label="Re-level Edge Clip Block028"
  AttacherType = Attacher::AttachEngine3D
  Height = 10
  Length = 20
  Placement = pos=(-19,-2,3) rot=(0,0,1;0rad)
  Width = 44
FEATURE [Part::Box] Box372  label="Cube306"
  AttacherType = Attacher::AttachEngine3D
  Height = 7
  Length = 10
  Placement = pos=(-15,34.6,-2) rot=(0,0,1;0rad)
  Width = 2
FEATURE [Part::Box] Box373  label="Cube307"
  AttacherType = Attacher::AttachEngine3D
  Height = 7
  Length = 10
  Placement = pos=(-15,25.4,-2) rot=(0,0,1;0rad)
  Width = 2
FEATURE [Part::MultiFuse] Fusion138
  Shapes = -> [Box361,Box364,Box369,Box373,Box372]
FEATURE [Part::Fuse] Fusion139  label="Bumps014"
  Base = -> Sphere115
  Tool = -> Sphere114
FEATURE [Part::Fuse] Fusion136
  Base = -> Fusion139
  Tool = -> Fusion138
FEATURE [Part::Sphere] Sphere117
  Angle1 = -90
  Angle2 = 90
  Angle3 = 360
  AttacherType = Attacher::AttachEngine3D
  Placement = pos=(-7.5,28,0.5) rot=(0,0,1;0rad)
  Radius = 1.5
FEATURE [Part::Fuse] Fusion140  label="Holes014"
  Base = -> Sphere117
  Tool = -> Sphere116
FEATURE [Part::Box] Box374  label="Re-level Edge Clip Block029"
  AttacherType = Attacher::AttachEngine3D
  Height = 10
  Length = 12
  Placement = pos=(-21.5,-2,-7) rot=(0,0,1;0rad)
  Width = 44
FEATURE [Part::Cut] Cut140
  Base = -> Fusion136
  Tool = -> Fusion140
FEATURE [Part::Cut] Cut141
  Base = -> Cut140
  Tool = -> Fusion137
FEATURE [Part::Cut] Cut142
  Base = -> Cut141
  Tool = -> Box371
FEATURE [Part::Cut] Cut143
  Base = -> Cut142
  Tool = -> Box374
FEATURE [Part::Cut] Cut144  label="Edge Clips010"
  Base = -> Cut143
  Placement = pos=(40,0,0) rot=(0,0,1;1.5708rad)
  Tool = -> Box363
FEATURE [Part::Box] Box375  label="Re-level Edge Clip Block030"
  AttacherType = Attacher::AttachEngine3D
  Height = 10
  Length = 12
  Placement = pos=(-21.5,-2,-7) rot=(0,0,1;0rad)
  Width = 44
FEATURE [Part::Box] Box376  label="Cube308"
  AttacherType = Attacher::AttachEngine3D
  Height = 7
  Length = 4
  Placement = pos=(-6,36.6,-2) rot=(0,0,1;0rad)
  Width = 1
FEATURE [Part::Box] Box377  label="Cube309"
  AttacherType = Attacher::AttachEngine3D
  Height = 7
  Length = 10
  Placement = pos=(-15,10,-2) rot=(0,0,1;0rad)
  Width = 2
FEATURE [Part::Box] Box378  label="Cube310"
  AttacherType = Attacher::AttachEngine3D
  Height = 7
  Length = 10
  Placement = pos=(-15,25.4,-2) rot=(0,0,1;0rad)
  Width = 2
FEATURE [Part::Box] Box379  label="Re-level Edge Clip Block031"
  AttacherType = Attacher::AttachEngine3D
  Height = 10
  Length = 20
  Placement = pos=(-19,-2,3) rot=(0,0,1;0rad)
  Width = 44
FEATURE [Part::Box] Box380  label="Cube311"
  AttacherType = Attacher::AttachEngine3D
  Height = 7
  Length = 10
  Placement = pos=(-15,34.6,-2) rot=(0,0,1;0rad)
  Width = 2
FEATURE [Part::Sphere] Sphere118
  Angle1 = -90
  Angle2 = 90
  Angle3 = 360
  AttacherType = Attacher::AttachEngine3D
  Placement = pos=(-7.5,34,0.5) rot=(0,0,1;0rad)
  Radius = 1.5
FEATURE [Part::Sphere] Sphere119
  Angle1 = -90
  Angle2 = 90
  Angle3 = 360
  AttacherType = Attacher::AttachEngine3D
  Placement = pos=(-7.5,28,0.5) rot=(0,0,1;0rad)
  Radius = 1.5
FEATURE [Part::Fuse] Fusion141  label="Holes015"
  Base = -> Sphere119
  Tool = -> Sphere118
FEATURE [Part::Box] Box381  label="Cube312"
  AttacherType = Attacher::AttachEngine3D
  Height = 7
  Length = 4
  Placement = pos=(-6,5,-2) rot=(0,0,1;0rad)
  Width = 1
FEATURE [Part::Box] Box382  label="Cube313"
  AttacherType = Attacher::AttachEngine3D
  Height = 7
  Length = 4
  Placement = pos=(-6,24.4,-2) rot=(0,0,1;0rad)
  Width = 1
FEATURE [Part::Sphere] Sphere120
  Angle1 = -90
  Angle2 = 90
  Angle3 = 360
  AttacherType = Attacher::AttachEngine3D
  Placement = pos=(-7.5,11.5,0.5) rot=(0,0,1;0rad)
  Radius = 1.25
FEATURE [Part::Box] Box383  label="Cube314"
  AttacherType = Attacher::AttachEngine3D
  Height = 7
  Length = 4
  Placement = pos=(-6,12,-2) rot=(0,0,1;0rad)
  Width = 1
FEATURE [Part::Box] Box384  label="Chamfer Cube015"
  AttacherType = Attacher::AttachEngine3D
  Height = 10
  Length = 13
  Placement = pos=(-11.69,0,-1.19) rot=(0,-1,0;0.785398rad)
  Width = 40
FEATURE [Part::Sphere] Sphere121
  Angle1 = -90
  Angle2 = 90
  Angle3 = 360
  AttacherType = Attacher::AttachEngine3D
  Placement = pos=(-7.5,6.5,0.5) rot=(0,0,1;0rad)
  Radius = 1.25
FEATURE [Part::Fuse] Fusion142  label="Bumps015"
  Base = -> Sphere121
  Tool = -> Sphere120
FEATURE [Part::Box] Box385  label="Cube315"
  AttacherType = Attacher::AttachEngine3D
  Height = 7
  Length = 5
  Placement = pos=(-5,0,-2) rot=(0,0,1;0rad)
  Width = 40
FEATURE [Part::Box] Box386  label="Cube316"
  AttacherType = Attacher::AttachEngine3D
  Height = 7
  Length = 4
  Placement = pos=(-6,27.4,-2) rot=(0,0,1;0rad)
  Width = 7.2
FEATURE [Part::Box] Box387  label="Cube317"
  AttacherType = Attacher::AttachEngine3D
  Height = 7
  Length = 4
  Placement = pos=(-6,8,-2) rot=(0,0,1;0rad)
  Width = 2
FEATURE [Part::MultiFuse] Fusion143  label="Extra Holes for Clips015"
  Shapes = -> [Box386,Box383,Box376,Box387,Box382,Box381]
FEATURE [Part::Box] Box388  label="Cube318"
  AttacherType = Attacher::AttachEngine3D
  Height = 7
  Length = 10
  Placement = pos=(-15,6,-2) rot=(0,0,1;0rad)
  Width = 2
FEATURE [Part::MultiFuse] Fusion144
  Shapes = -> [Box385,Box388,Box377,Box378,Box380]
FEATURE [Part::Fuse] Fusion145
  Base = -> Fusion142
  Tool = -> Fusion144
FEATURE [Part::Cut] Cut146
  Base = -> Fusion145
  Tool = -> Fusion141
FEATURE [Part::Cut] Cut147
  Base = -> Cut146
  Tool = -> Fusion143
FEATURE [Part::Cut] Cut148
  Base = -> Cut147
  Tool = -> Box379
FEATURE [Part::Cut] Cut149
  Base = -> Cut148
  Tool = -> Box375
FEATURE [Part::Cut] Cut145  label="Edge Clips011"
  Base = -> Cut149
  Placement = pos=(40,40,0) rot=(0,0,1;3.14159rad)
  Tool = -> Box384
FEATURE [Part::Box] Box389  label="Re-level Edge Clip Block032"
  AttacherType = Attacher::AttachEngine3D
  Height = 10
  Length = 12
  Placement = pos=(-21.5,-2,-7) rot=(0,0,1;0rad)
  Width = 44
FEATURE [Part::Box] Box390  label="Cube319"
  AttacherType = Attacher::AttachEngine3D
  Height = 7
  Length = 10
  Placement = pos=(-15,10,-2) rot=(0,0,1;0rad)
  Width = 2
FEATURE [Part::Box] Box391  label="Cube320"
  AttacherType = Attacher::AttachEngine3D
  Height = 7
  Length = 4
  Placement = pos=(-6,12,-2) rot=(0,0,1;0rad)
  Width = 1
FEATURE [Part::Box] Box392  label="Chamfer Cube016"
  AttacherType = Attacher::AttachEngine3D
  Height = 10
  Length = 13
  Placement = pos=(-11.69,0,-1.19) rot=(0,-1,0;0.785398rad)
  Width = 40
FEATURE [Part::Sphere] Sphere122
  Angle1 = -90
  Angle2 = 90
  Angle3 = 360
  AttacherType = Attacher::AttachEngine3D
  Placement = pos=(-7.5,6.5,0.5) rot=(0,0,1;0rad)
  Radius = 1.25
FEATURE [Part::Box] Box393  label="Cube321"
  AttacherType = Attacher::AttachEngine3D
  Height = 7
  Length = 5
  Placement = pos=(-5,0,-2) rot=(0,0,1;0rad)
  Width = 40
FEATURE [Part::Box] Box394  label="Cube322"
  AttacherType = Attacher::AttachEngine3D
  Height = 7
  Length = 4
  Placement = pos=(-6,27.4,-2) rot=(0,0,1;0rad)
  Width = 7.2
FEATURE [Part::Box] Box395  label="Cube323"
  AttacherType = Attacher::AttachEngine3D
  Height = 7
  Length = 4
  Placement = pos=(-6,8,-2) rot=(0,0,1;0rad)
  Width = 2
FEATURE [Part::Box] Box396  label="Cube324"
  AttacherType = Attacher::AttachEngine3D
  Height = 7
  Length = 10
  Placement = pos=(-15,6,-2) rot=(0,0,1;0rad)
  Width = 2
FEATURE [Part::Sphere] Sphere123
  Angle1 = -90
  Angle2 = 90
  Angle3 = 360
  AttacherType = Attacher::AttachEngine3D
  Placement = pos=(-7.5,28,0.5) rot=(0,0,1;0rad)
  Radius = 1.5
FEATURE [Part::Box] Box397  label="Cube325"
  AttacherType = Attacher::AttachEngine3D
  Height = 7
  Length = 4
  Placement = pos=(-6,5,-2) rot=(0,0,1;0rad)
  Width = 1
FEATURE [Part::Box] Box398  label="Cube326"
  AttacherType = Attacher::AttachEngine3D
  Height = 7
  Length = 4
  Placement = pos=(-6,24.4,-2) rot=(0,0,1;0rad)
  Width = 1
FEATURE [Part::Sphere] Sphere124
  Angle1 = -90
  Angle2 = 90
  Angle3 = 360
  AttacherType = Attacher::AttachEngine3D
  Placement = pos=(-7.5,11.5,0.5) rot=(0,0,1;0rad)
  Radius = 1.25
FEATURE [Part::Box] Box399  label="Re-level Edge Clip Block033"
  AttacherType = Attacher::AttachEngine3D
  Height = 10
  Length = 20
  Placement = pos=(-19,-2,3) rot=(0,0,1;0rad)
  Width = 44
FEATURE [Part::Box] Box400  label="Cube327"
  AttacherType = Attacher::AttachEngine3D
  Height = 7
  Length = 10
  Placement = pos=(-15,34.6,-2) rot=(0,0,1;0rad)
  Width = 2
FEATURE [Part::Box] Box401  label="Cube328"
  AttacherType = Attacher::AttachEngine3D
  Height = 7
  Length = 10
  Placement = pos=(-15,25.4,-2) rot=(0,0,1;0rad)
  Width = 2
FEATURE [Part::MultiFuse] Fusion148
  Shapes = -> [Box393,Box396,Box390,Box401,Box400]
FEATURE [Part::Box] Box402  label="Cube329"
  AttacherType = Attacher::AttachEngine3D
  Height = 7
  Length = 4
  Placement = pos=(-6,36.6,-2) rot=(0,0,1;0rad)
  Width = 1
FEATURE [Part::MultiFuse] Fusion147  label="Extra Holes for Clips016"
  Shapes = -> [Box394,Box391,Box402,Box395,Box398,Box397]
FEATURE [Part::Fuse] Fusion150  label="Bumps016"
  Base = -> Sphere122
  Tool = -> Sphere124
FEATURE [Part::Fuse] Fusion146
  Base = -> Fusion150
  Tool = -> Fusion148
FEATURE [Part::Sphere] Sphere125
  Angle1 = -90
  Angle2 = 90
  Angle3 = 360
  AttacherType = Attacher::AttachEngine3D
  Placement = pos=(-7.5,34,0.5) rot=(0,0,1;0rad)
  Radius = 1.5
FEATURE [Part::Fuse] Fusion149  label="Holes016"
  Base = -> Sphere123
  Tool = -> Sphere125
FEATURE [Part::Cut] Cut154
  Base = -> Fusion146
  Tool = -> Fusion149
FEATURE [Part::Cut] Cut150
  Base = -> Cut154
  Tool = -> Fusion147
FEATURE [Part::Cut] Cut151
  Base = -> Cut150
  Tool = -> Box399
FEATURE [Part::Cut] Cut152
  Base = -> Cut151
  Tool = -> Box389
FEATURE [Part::Cut] Cut153  label="Edge Clips012"
  Base = -> Cut152
  Placement = pos=(0,40,0) rot=(0,0,-1;1.5708rad)
  Tool = -> Box392
FEATURE [Part::Cut] Cut155
  Base = -> Box342
  Tool = -> Fusion130
FEATURE [Part::Box] Box403  label="Cube330"
  AttacherType = Attacher::AttachEngine3D
  Height = 10
  Length = 10
  Placement = pos=(24,-6,1) rot=(0.205904,-0.974848,-0.085288;0.803573rad)
  Width = 15
FEATURE [Part::Box] Box404  label="Cube331"
  AttacherType = Attacher::AttachEngine3D
  Height = 10
  Length = 10
  Placement = pos=(-6,16,1) rot=(-0.273007,-0.419215,-0.865867;1.78566rad)
  Width = 15
FEATURE [Part::Box] Box405  label="Cube332"
  AttacherType = Attacher::AttachEngine3D
  Height = 10
  Length = 10
  Placement = pos=(16,46,1) rot=(0.381439,0.080566,0.920876;3.07487rad)
  Width = 15
FEATURE [Part::Box] Box406  label="Cube333"
  AttacherType = Attacher::AttachEngine3D
  Height = 10
  Length = 10
  Placement = pos=(46,24,1) rot=(0.442189,-0.287968,0.849437;1.66134rad)
  Width = 15
FEATURE [Part::MultiFuse] Fusion151  label="Glue Dents003"
  Shapes = -> [Box403,Box404,Box405,Box406]
FEATURE [Part::MultiFuse] Fusion152
  Shapes = -> [Cut153,Cut139,Cut144,Cut145]
FEATURE [Part::Fuse] Fusion153
  Base = -> Cut155
  Tool = -> Fusion152
FEATURE [Part::Cut] Cut156  label="Nut Plate002"
  Base = -> Fusion153
  Tool = -> Fusion151
FEATURE [Part::Cut] Cut157
  Base = -> Cut156
  Tool = -> Chamfer018
FEATURE [Part::Cut] Cut158
  Base = -> Cut157
  Tool = -> Chamfer017
FEATURE [Part::Cut] Cut159  label="Nut Plate003"
  Base = -> Cut158
  Placement = pos=(29.98,40,7) rot=(1,0,0;3.14159rad)
  Tool = -> Box343
FEATURE [Part::Cylinder] Cylinder038
  Angle = 360
  AttacherType = Attacher::AttachEngine3D
  Height = 10
  Placement = pos=(63.97,34,0) rot=(0,0,1;0rad)
  Radius = 1.5
FEATURE [Part::Cylinder] Cylinder039
  Angle = 360
  AttacherType = Attacher::AttachEngine3D
  Height = 10
  Placement = pos=(65.97,34,0) rot=(0,0,1;0rad)
  Radius = 1.5
note: 1 file-system path scrubbed to <path> (originals preserved in the JSON sidecar)
